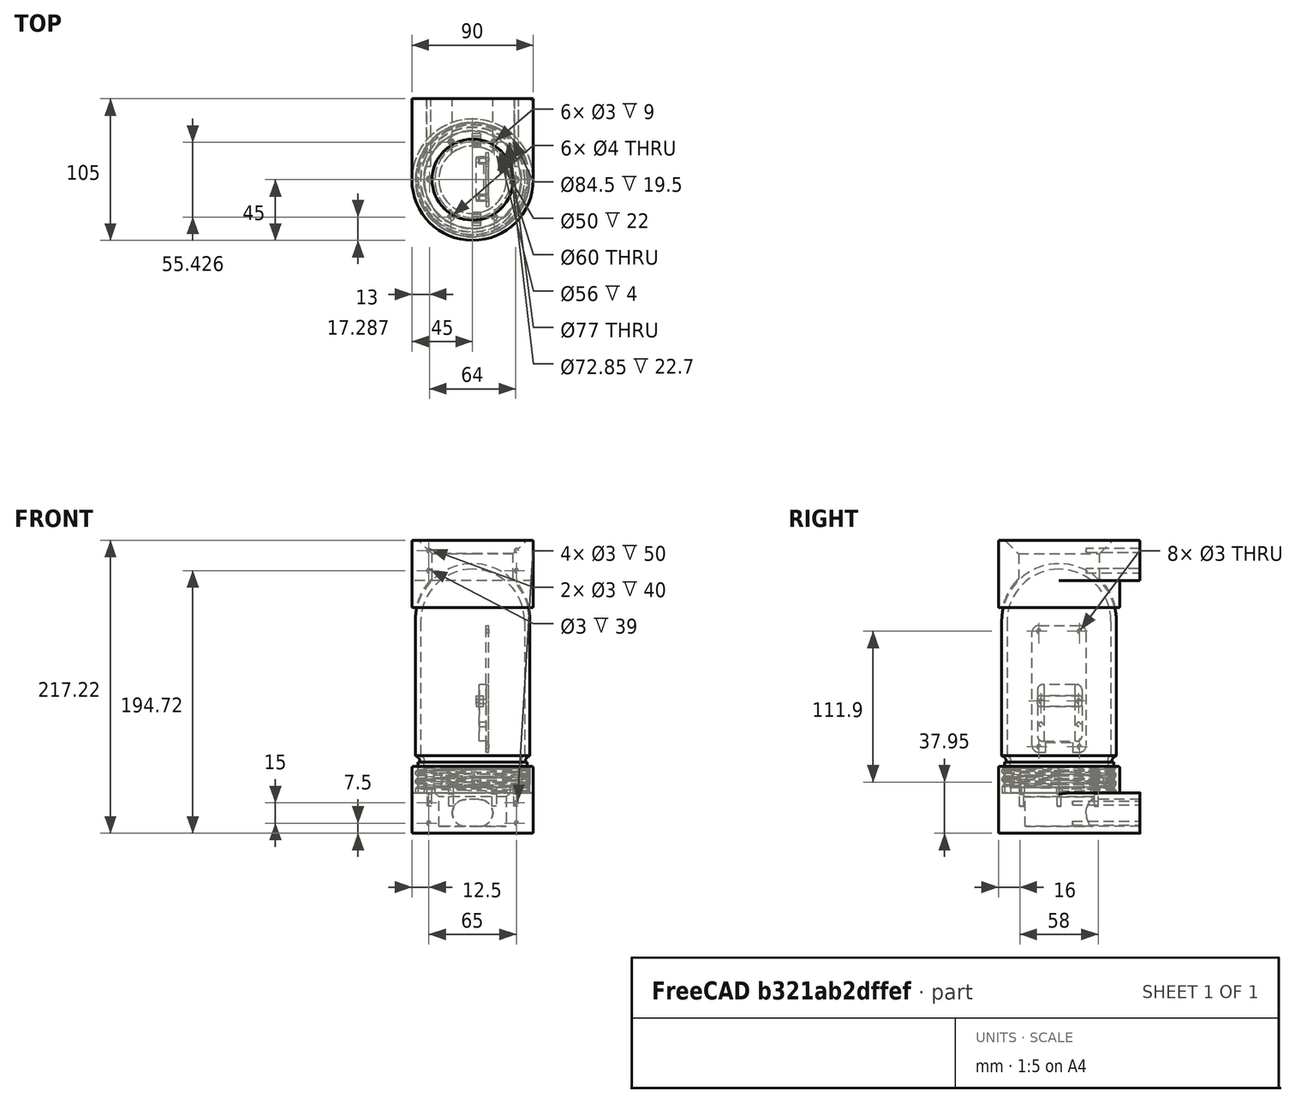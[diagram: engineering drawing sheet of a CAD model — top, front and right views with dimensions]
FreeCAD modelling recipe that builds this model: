
FCSTD DOCUMENT  (FreeCAD 0.20R)
Label: CrocSaintGerard_V6
License: All rights reserved
LicenseURL: http://en.wikipedia.org/wiki/All_rights_reserved
objects: Sketcher::SketchObject×46, PartDesign::Pocket×23, PartDesign::Fillet×21, PartDesign::Pad×19, PartDesign::Body×17, PartDesign::Chamfer×5, Mesh::Feature×4, TechDraw::DrawSVGTemplate×3, TechDraw::DrawViewPart×3, TechDraw::DrawPage×3, PartDesign::Revolution×2, Part::Helix×1, PartDesign::ShapeBinder×1, PartDesign::AdditivePipe×1, PartDesign::LinearPattern×1, PartDesign::Groove×1, App::VRMLObject×1, App::MeasureDistance×1
note: 210 computed .brp shape members not serialized (recipe doc carries the construction recipe); baked Part::Feature solids carry a one-line shape summary decoded from their .brp

FEATURE [Part::Helix] Helix
  Angle = 0
  AttacherType = Attacher::AttachEngine3D
  Height = 6.22
  LocalCoord = 0
  Pitch = 6.23
  Radius = 40.5
  SegmentLength = 1
  Style = 1
FEATURE [Sketcher::SketchObject] Sketch001  label="sketch_cylindre_base"
  FullyConstrained = true
  MapMode = 5
  Support = -> [XY_Plane]
  sketch-geometry (2):
    g0: Circle CenterX=0 CenterY=0 CenterZ=0 NormalX=0 NormalY=0 NormalZ=1 AngleXU=0 Radius=42.25
    g1: Circle CenterX=0 CenterY=0 CenterZ=0 NormalX=0 NormalY=0 NormalZ=1 AngleXU=0 Radius=45
  constraints (4):
    c: Coincident(g0,g-1)
    c: Coincident(g1,g0)
    c: Radius(g0) = 42.25
    c: Radius(g1) = 45
FEATURE [PartDesign::Pad] Pad  label="cylindre_base"
  Direction = (1,1,1)
  Length = 20
  Length2 = 100
  Profile = -> Sketch001
  Type = 0
FEATURE [Sketcher::SketchObject] Sketch002  label="sketch_profil_dent"
  FullyConstrained = true
  MapMode = 5
  Placement = pos=(0,0,0) rot=(1,0,0;1.5708rad)
  Support = -> [XZ_Plane]
  sketch-geometry (7):
    g0: LineSegment StartX=42.25 StartY=4.40427 StartZ=0 EndX=40.9557 EndY=3.11 EndZ=0
    g1: LineSegment StartX=40.9557 StartY=3.11 StartZ=0 EndX=40.9557 EndY=1.29427 EndZ=0
    g2: LineSegment StartX=40.9557 StartY=1.29427 StartZ=0 EndX=42.25 EndY=0 EndZ=0
    g3: LineSegment StartX=42.25 StartY=4.40427 StartZ=0 EndX=42.25 EndY=6.22 EndZ=0
    g4: LineSegment StartX=42.25 StartY=6.22 StartZ=0 EndX=43.25 EndY=6.22 EndZ=0
    g5: LineSegment StartX=43.25 StartY=6.22 StartZ=0 EndX=43.25 EndY=0 EndZ=0
    g6: LineSegment StartX=43.25 StartY=0 StartZ=0 EndX=42.25 EndY=0 EndZ=0
  constraints (21):
    c: Coincident(g0,g1)
    c: Vertical(g1)
    c: Coincident(g1,g2)
    c: DistanceX(g-2,g2) = 42.25
    c: PointOnObject(g2,g-1)
    c: Coincident(g0,g3)
    c: Vertical(g3)
    c: Coincident(g3,g4)
    c: Horizontal(g4)
    c: Coincident(g4,g5)
    c: PointOnObject(g5,g-1)
    c: Vertical(g5)
    c: Coincident(g5,g6)
    c: Coincident(g6,g2)
    c: DistanceX(g4,g4) = 1
    c: Equal(g3,g1)
    c: Equal(g2,g0)
    c: Angle(g2,g-1) = 0.785398
    c: Equal(g1,g3)
    c: DistanceY(g5,g5) = 6.22
    c: DistanceX(g-2,g0) = 42.25
FEATURE [PartDesign::ShapeBinder] ShapeBinder  label="ShapeBinder-helix"
  Support = -> [Helix]
  TraceSupport = false
FEATURE [PartDesign::AdditivePipe] AdditivePipe  label="filet"
  AuxilleryCurvelinear = true
  AuxillerySpineTangent = false
  BaseFeature = -> Pad
  Binormal = (0,0,0)
  Mode = 2
  Profile = -> Sketch002
  Spine = -> ShapeBinder
  SpineTangent = false
  Transformation = 0
  Transition = 0
FEATURE [PartDesign::LinearPattern] LinearPattern  label="ajout_filets"
  BaseFeature = -> AdditivePipe
  Direction = -> Z_Axis
  Length = 12.46
  Occurrences = 3
  Originals = -> [AdditivePipe]
  Overlap = 0
FEATURE [Sketcher::SketchObject] Sketch003  label="sketch_decoupe_filetage"
  FullyConstrained = true
  MapMode = 5
  Placement = pos=(0,0,0) rot=(1,0,0;1.5708rad)
  Support = -> [XZ_Plane]
  sketch-geometry (4):
    g0: LineSegment StartX=-90 StartY=29.5 StartZ=0 EndX=90 EndY=29.5 EndZ=0
    g1: LineSegment StartX=90 StartY=29.5 StartZ=0 EndX=90 EndY=19.5 EndZ=0
    g2: LineSegment StartX=90 StartY=19.5 StartZ=0 EndX=-90 EndY=19.5 EndZ=0
    g3: LineSegment StartX=-90 StartY=19.5 StartZ=0 EndX=-90 EndY=29.5 EndZ=0
  constraints (11):
    c: Coincident(g0,g1)
    c: Coincident(g1,g2)
    c: Coincident(g2,g3)
    c: Coincident(g3,g0)
    c: Horizontal(g2)
    c: Vertical(g1)
    c: Vertical(g3)
    c: DistanceY(g-1,g1) = 19.5
    c: Symmetric(g0,g0,g-2)
    c: DistanceY(g1,g1) = 10
    c: DistanceX(g0,g0) = 180
FEATURE [PartDesign::Pocket] Pocket  label="decoupe_filetage"
  BaseFeature = -> LinearPattern
  Length = 200
  Length2 = 100
  Midplane = true
  Profile = -> Sketch003
  Type = 0
FEATURE [Sketcher::SketchObject] Sketch008  label="sketch_enceinte_verre"
  FullyConstrained = true
  MapMode = 5
  Support = -> [XY_Plane003]
  sketch-geometry (11):
    g0: ArcOfCircle CenterX=-127.4 CenterY=0 CenterZ=0 NormalX=0 NormalY=0 NormalZ=1 AngleXU=0 Radius=42.5 StartAngle=1.5708 EndAngle=3.14159
    g1: ArcOfCircle CenterX=-127.4 CenterY=0 CenterZ=0 NormalX=0 NormalY=0 NormalZ=1 AngleXU=0 Radius=38.5 StartAngle=1.5708 EndAngle=3.14159
    g2: LineSegment StartX=-127.4 StartY=38.5 StartZ=0 EndX=-27.4 EndY=38.5 EndZ=0
    g3: ArcOfCircle CenterX=-24.2871 CenterY=39.1905 CenterZ=0 NormalX=0 NormalY=0 NormalZ=1 AngleXU=0 Radius=3.18854 StartAngle=3.35987 EndAngle=5.2334
    g4: LineSegment StartX=-22.7 StartY=36.425 StartZ=0 EndX=0 EndY=36.425 EndZ=0
    g5: LineSegment StartX=-127.4 StartY=42.5 StartZ=0 EndX=-27.4 EndY=42.5 EndZ=0
    g6: ArcOfCircle CenterX=-22.7 CenterY=43.802 CenterZ=0 NormalX=0 NormalY=0 NormalZ=1 AngleXU=0 Radius=4.87701 StartAngle=3.41184 EndAngle=4.71239
    g7: LineSegment StartX=-22.7 StartY=38.925 StartZ=0 EndX=-22.7 EndY=40.425 EndZ=0
    g8: LineSegment StartX=-22.7 StartY=40.425 StartZ=0 EndX=0 EndY=40.425 EndZ=0
    g9: LineSegment StartX=0 StartY=40.425 StartZ=0 EndX=0 EndY=36.425 EndZ=0
    g10: LineSegment StartX=-165.9 StartY=4.7e-15 StartZ=0 EndX=-169.9 EndY=5.2e-15 EndZ=0
  constraints (35):
    c: PointOnObject(g0,g-1)
    c: PointOnObject(g0,g-1)
    c: Coincident(g1,g0)
    c: PointOnObject(g1,g-1)
    c: Angle(g1) = 1.5708
    c: Angle(g0) = 1.5708
    c: Tangent(g1,g2) = 1.5708
    c: Coincident(g3,g2)
    c: Coincident(g4,g3)
    c: PointOnObject(g4,g-2)
    c: Horizontal(g4)
    c: Coincident(g5,g0)
    c: Horizontal(g5)
    c: Coincident(g6,g5)
    c: Coincident(g6,g7)
    c: Coincident(g7,g8)
    c: PointOnObject(g8,g-2)
    c: Horizontal(g8)
    c: Coincident(g8,g9)
    c: Coincident(g9,g4)
    c: Coincident(g10,g0)
    c: DistanceX(g10,g10) = 4
    c: Radius(g0) = 42.5
    c: Coincident(g1,g10)
    c: DistanceY(g9,g9) = 4
    c: Perpendicular(g6,g7)
    c: Vertical(g7)
    c: DistanceY(g-1,g4) = 36.425
    c: Equal(g4,g8)
    c: DistanceX(g8,g8) = 22.7
    c: DistanceX(g-2,g5) = -27.4
    c: Equal(g2,g5)
    c: PointOnObject(g3,g6)
    c: DistanceY(g7,g7) = 1.5
    c: DistanceX(g5,g5) = 100
FEATURE [PartDesign::Revolution] Revolution  label="revolution_enceinte_verre"
  AllowMultiFace = false
  Angle = 360
  Axis = (1,0,0)
  Base = (0,0,0)
  Profile = -> Sketch008
  ReferenceAxis = -> Sketch008 [H_Axis]
FEATURE [PartDesign::Body] Body003  label="enceinte_verre"
  Group = -> [Sketch008,Revolution]
  Origin = -> Origin003
  Placement = pos=(-3.8e-15,0,-1.78e-14) rot=(0,1,0;1.5708rad)
  Tip = -> Revolution
FEATURE [Sketcher::SketchObject] Sketch  label="sketch_base"
  ExternalGeometry = -> [Pocket]
  FullyConstrained = true
  MapMode = 5
  Placement = pos=(0,0,0) rot=(1,0,0;3.14159rad)
  Support = -> [Pocket]
  sketch-geometry (4):
    g0: ArcOfCircle CenterX=0 CenterY=0 CenterZ=0 NormalX=0 NormalY=0 NormalZ=1 AngleXU=0 Radius=45 StartAngle=0 EndAngle=3.14159
    g1: LineSegment StartX=-45 StartY=5.5e-15 StartZ=0 EndX=-45 EndY=-60 EndZ=0
    g2: LineSegment StartX=-45 StartY=-60 StartZ=0 EndX=45 EndY=-60 EndZ=0
    g3: LineSegment StartX=45 StartY=-60 StartZ=0 EndX=45 EndY=0 EndZ=0
  constraints (11):
    c: Coincident(g0,g-1)
    c: PointOnObject(g0,g-1)
    c: PointOnObject(g0,g-1)
    c: Tangent(g0,g1) = -1.5708
    c: Coincident(g1,g2)
    c: Horizontal(g2)
    c: Coincident(g2,g3)
    c: Coincident(g3,g0)
    c: Vertical(g3)
    c: Radius(g0) = 45
    c: DistanceY(g1,g1) = 60
FEATURE [PartDesign::Pad] Pad001  label="base"
  BaseFeature = -> Pocket
  Direction = (1,1,1)
  Length = 30
  Length2 = 100
  Profile = -> Sketch
  Type = 0
FEATURE [Sketcher::SketchObject] Sketch009  label="sketch_passage_fils"
  FullyConstrained = true
  MapMode = 5
  Support = -> [Pad001]
  sketch-geometry (1):
    g0: Circle CenterX=0 CenterY=0 CenterZ=0 NormalX=0 NormalY=0 NormalZ=1 AngleXU=0 Radius=25
  constraints (2):
    c: Coincident(g0,g-1)
    c: Radius(g0) = 25
FEATURE [PartDesign::Pocket] Pocket001  label="passage_fils"
  BaseFeature = -> Pad001
  Length = 25
  Length2 = 100
  Profile = -> Sketch009
  Type = 0
FEATURE [Sketcher::SketchObject] Sketch010  label="sketch_passage_fils_vertical"
  ExternalGeometry = -> [Pocket001]
  FullyConstrained = true
  MapMode = 5
  Placement = pos=(0,60,0) rot=(0,0.707107,0.707107;3.14159rad)
  Support = -> [Pocket001]
  sketch-geometry (4):
    g0: ArcOfCircle CenterX=-5 CenterY=-15 CenterZ=0 NormalX=0 NormalY=0 NormalZ=1 AngleXU=0 Radius=10 StartAngle=1.5708 EndAngle=4.71239
    g1: ArcOfCircle CenterX=5 CenterY=-15 CenterZ=0 NormalX=0 NormalY=0 NormalZ=1 AngleXU=0 Radius=10 StartAngle=4.71239 EndAngle=7.85398
    g2: LineSegment StartX=-5 StartY=-25 StartZ=0 EndX=5 EndY=-25 EndZ=0
    g3: LineSegment StartX=-5 StartY=-5 StartZ=0 EndX=5 EndY=-5 EndZ=0
  constraints (9):
    c: Tangent(g0,g3) = 1.5708
    c: Tangent(g0,g2) = -1.5708
    c: Tangent(g2,g1) = -1.5708
    c: Tangent(g3,g1) = 1.5708
    c: Equal(g0,g1)
    c: Symmetric(g0,g1,g-2)
    c: Distance(g1,g-3) = 5
    c: DistanceY(g-1,g1) = -5
    c: DistanceX(g2,g2) = 10
FEATURE [PartDesign::Pocket] Pocket002  label="passage_fils_vertical"
  BaseFeature = -> Pocket001
  Length = 60
  Length2 = 100
  Profile = -> Sketch010
  Type = 0
FEATURE [Sketcher::SketchObject] Sketch011  label="sketch_vis_fixation"
  ExternalGeometry = -> [Pocket002]
  FullyConstrained = true
  MapMode = 5
  Placement = pos=(0,60,0) rot=(0,0.707107,0.707107;3.14159rad)
  Support = -> [Pocket002]
  sketch-geometry (4):
    g0: Circle CenterX=-32.5 CenterY=-7.5 CenterZ=0 NormalX=0 NormalY=0 NormalZ=1 AngleXU=0 Radius=1.5
    g1: Circle CenterX=32.5 CenterY=-7.5 CenterZ=0 NormalX=0 NormalY=0 NormalZ=1 AngleXU=0 Radius=1.5
    g2: Circle CenterX=-32.5 CenterY=-22.5 CenterZ=0 NormalX=0 NormalY=0 NormalZ=1 AngleXU=0 Radius=1.5
    g3: Circle CenterX=32.5 CenterY=-22.5 CenterZ=0 NormalX=0 NormalY=0 NormalZ=1 AngleXU=0 Radius=1.5
  constraints (10):
    c: Symmetric(g1,g0,g-2)
    c: DistanceY(g-1,g0) = -7.5
    c: Distance(g0,g1) = 65
    c: Radius(g0) = 1.5
    c: Equal(g0,g1)
    c: Symmetric(g3,g2,g-2)
    c: Radius(g2) = 1.5
    c: Equal(g2,g3)
    c: Distance(g3,g2) = 65
    c: Distance(g3,g-3) = 7.5
FEATURE [PartDesign::Pocket] Pocket003  label="vis_fixation"
  BaseFeature = -> Pocket002
  Length = 50
  Length2 = 100
  Profile = -> Sketch011
  Type = 0
FEATURE [PartDesign::Chamfer] Chamfer
  Angle = 45
  Base = -> Pocket003 [Edge95]
  BaseFeature = -> Pocket003
  ChamferType = 0
  FlipDirection = false
  Size = 3
  Size2 = 1
  SupportTransform = false
FEATURE [Sketcher::SketchObject] Sketch012  label="sketch_vis_montage_interieur"
  FullyConstrained = true
  MapMode = 5
  Support = -> [Chamfer]
  sketch-geometry (13):
    g0: LineSegment StartX=-16 StartY=27.7128 StartZ=0 EndX=-32 EndY=-3.3857e-12 EndZ=0
    g1: LineSegment StartX=-32 StartY=-3.3857e-12 StartZ=0 EndX=-16 EndY=-27.7128 EndZ=0
    g2: LineSegment StartX=-16 StartY=-27.7128 StartZ=0 EndX=16 EndY=-27.7128 EndZ=0
    g3: LineSegment StartX=16 StartY=-27.7128 StartZ=0 EndX=32 EndY=9.738e-12 EndZ=0
    g4: LineSegment StartX=32 StartY=9.738e-12 StartZ=0 EndX=16 EndY=27.7128 EndZ=0
    g5: LineSegment StartX=16 StartY=27.7128 StartZ=0 EndX=-16 EndY=27.7128 EndZ=0
    g6: Circle CenterX=0 CenterY=0 CenterZ=0 NormalX=0 NormalY=0 NormalZ=1 AngleXU=0 Radius=32
    g7: Circle CenterX=-16 CenterY=27.7128 CenterZ=0 NormalX=0 NormalY=0 NormalZ=1 AngleXU=0 Radius=1.5
    g8: Circle CenterX=16 CenterY=27.7128 CenterZ=0 NormalX=0 NormalY=0 NormalZ=1 AngleXU=0 Radius=1.5
    g9: Circle CenterX=-32 CenterY=-3.3857e-12 CenterZ=0 NormalX=0 NormalY=0 NormalZ=1 AngleXU=0 Radius=1.5
    g10: Circle CenterX=32 CenterY=9.738e-12 CenterZ=0 NormalX=0 NormalY=0 NormalZ=1 AngleXU=0 Radius=1.5
    g11: Circle CenterX=16 CenterY=-27.7128 CenterZ=0 NormalX=0 NormalY=0 NormalZ=1 AngleXU=0 Radius=1.5
    g12: Circle CenterX=-16 CenterY=-27.7128 CenterZ=0 NormalX=0 NormalY=0 NormalZ=1 AngleXU=0 Radius=1.5
  constraints (28):
    c: Coincident(g0,g1)
    c: Coincident(g1,g2)
    c: Coincident(g2,g3)
    c: Coincident(g3,g4)
    c: Coincident(g4,g5)
    c: Coincident(g5,g0)
    c: Equal(g0, g1-g5) x5
    c: PointOnObject(g0,g6)
    c: PointOnObject(g1,g6)
    c: PointOnObject(g2,g6)
    c: PointOnObject(g3,g6)
    c: PointOnObject(g4,g6)
    c: PointOnObject(g5,g6)
    c: Coincident(g6,g-1)
    c: Horizontal(g5)
    c: Radius(g6) = 32
    c: Coincident(g7,g0)
    c: Coincident(g8,g4)
    c: Coincident(g9,g0)
    c: Coincident(g10,g3)
    c: Coincident(g11,g2)
    c: Coincident(g12,g1)
    c: Radius(g11) = 1.5
    c: Equal(g11,g12)
    c: Equal(g11,g9)
    c: Equal(g11,g7)
    c: Equal(g11,g8)
    c: Equal(g11,g10)
FEATURE [PartDesign::Pocket] Pocket004  label="vis_montage_interieur"
  BaseFeature = -> Chamfer
  Length = 10
  Length2 = 100
  Profile = -> Sketch012
  Type = 0
FEATURE [PartDesign::Chamfer] Chamfer001
  Angle = 45
  Base = -> Pocket004 [Edge3,Edge2,Edge4,Edge6,Edge8,Edge7]
  BaseFeature = -> Pocket004
  ChamferType = 0
  FlipDirection = false
  Size = 1
  Size2 = 1
  SupportTransform = false
FEATURE [Mesh::Feature] Mesh  label="fixation_enceinte_verre (Meshed)"
FEATURE [Sketcher::SketchObject] Sketch013
  FullyConstrained = true
  MapMode = 5
  Placement = pos=(0,0,0) rot=(0.57735,0.57735,0.57735;2.0944rad)
  Support = -> [YZ_Plane004]
  sketch-geometry (4):
    g0: ArcOfCircle CenterX=0 CenterY=128 CenterZ=0 NormalX=0 NormalY=0 NormalZ=1 AngleXU=0 Radius=43 StartAngle=2.39448 EndAngle=2.92551
    g1: LineSegment StartX=-42 StartY=137.22 StartZ=0 EndX=-45 EndY=137.22 EndZ=0
    g2: LineSegment StartX=-45 StartY=137.22 StartZ=0 EndX=-45 EndY=157.22 EndZ=0
    g3: LineSegment StartX=-45 StartY=157.22 StartZ=0 EndX=-31.5471 EndY=157.22 EndZ=0
  constraints (13):
    c: PointOnObject(g0,g-2)
    c: Coincident(g0,g1)
    c: Coincident(g1,g2)
    c: Vertical(g2)
    c: Coincident(g2,g3)
    c: Coincident(g3,g0)
    c: Horizontal(g3)
    c: Horizontal(g1)
    c: Radius(g0) = 43
    c: DistanceY(g2,g2) = 20
    c: DistanceX(g-2,g1) = -45
    c: DistanceY(g-1,g0) = 128
    c: DistanceX(g1,g1) = 3
FEATURE [PartDesign::Revolution] Revolution001
  Angle = 360
  Axis = (-2e-16,3e-16,1)
  Base = (0,0,0)
  Placement = pos=(0,0,0) rot=(0.57735,0.57735,0.57735;2.0944rad)
  Profile = -> Sketch013
  ReferenceAxis = -> Sketch013 [V_Axis]
FEATURE [Sketcher::SketchObject] Sketch014
  ExternalGeometry = -> [Revolution001]
  FullyConstrained = true
  MapMode = 5
  Placement = pos=(-6.92e-14,4.4e-14,157.22) rot=(0,0,-1;1.5708rad)
  Support = -> [Revolution001]
  sketch-geometry (4):
    g0: ArcOfCircle CenterX=0 CenterY=0 CenterZ=0 NormalX=0 NormalY=0 NormalZ=1 AngleXU=0 Radius=45 StartAngle=4.71239 EndAngle=7.85398
    g1: LineSegment StartX=1.38e-14 StartY=45 StartZ=0 EndX=-60 EndY=45 EndZ=0
    g2: LineSegment StartX=-60 StartY=45 StartZ=0 EndX=-60 EndY=-45 EndZ=0
    g3: LineSegment StartX=-60 StartY=-45 StartZ=0 EndX=-7.1e-15 EndY=-45 EndZ=0
  constraints (10):
    c: Coincident(g0,g-1)
    c: PointOnObject(g0,g-3)
    c: PointOnObject(g0,g-2)
    c: PointOnObject(g0,g-2)
    c: Tangent(g0,g1) = -1.5708
    c: Coincident(g1,g2)
    c: Coincident(g2,g3)
    c: Coincident(g3,g0)
    c: Symmetric(g2,g1,g-1)
    c: DistanceX(g-2,g1) = -60
FEATURE [PartDesign::Pad] Pad002
  BaseFeature = -> Revolution001
  Direction = (1,1,1)
  Length = 30
  Length2 = 100
  Placement = pos=(0,0,0) rot=(0.57735,0.57735,0.57735;2.0944rad)
  Profile = -> Sketch014
  Type = 0
FEATURE [Sketcher::SketchObject] Sketch015
  ExternalGeometry = -> [Pad002]
  FullyConstrained = true
  MapMode = 5
  Placement = pos=(0,0,0) rot=(0.57735,0.57735,0.57735;2.0944rad)
  Support = -> [YZ_Plane004]
  sketch-geometry (3):
    g0: ArcOfCircle CenterX=2.84e-14 CenterY=128 CenterZ=0 NormalX=0 NormalY=0 NormalZ=1 AngleXU=0 Radius=43 StartAngle=1.5708 EndAngle=2.39448
    g1: LineSegment StartX=-31.5471 StartY=157.22 StartZ=0 EndX=3.6e-15 EndY=157.22 EndZ=0
    g2: LineSegment StartX=3.6e-15 StartY=157.22 StartZ=0 EndX=3.6e-15 EndY=171 EndZ=0
  constraints (8):
    c: Coincident(g0,g-3)
    c: Coincident(g0,g-3)
    c: PointOnObject(g0,g-2)
    c: Coincident(g0,g1)
    c: Coincident(g1,g2)
    c: Coincident(g2,g0)
    c: Vertical(g2)
    c: Horizontal(g1)
FEATURE [PartDesign::Groove] Groove
  Angle = 360
  Axis = (-2e-16,3e-16,1)
  Base = (0,0,0)
  BaseFeature = -> Pad002
  Placement = pos=(0,0,0) rot=(0.57735,0.57735,0.57735;2.0944rad)
  Profile = -> Sketch015
  ReferenceAxis = -> Sketch015 [V_Axis]
  Reversed = true
FEATURE [PartDesign::Fillet] Fillet
  Base = -> Chamfer001 [Edge116,Edge168,Edge182,Edge171,Edge181,Edge166]
  BaseFeature = -> Chamfer001
  Radius = 1
  SupportTransform = false
FEATURE [PartDesign::Body] Body  label="fixation_enceinte_verre"
  Group = -> [Sketch001,Pad,Sketch002,ShapeBinder,AdditivePipe,LinearPattern,Sketch003,Pocket,Sketch,Pad001,Sketch009,Pocket001,Sketch010,Pocket002,Sketch011,Pocket003,Chamfer,Sketch012,Pocket004,Chamfer001,Fillet]
  Origin = -> Origin
  Tip = -> Fillet
FEATURE [Sketcher::SketchObject] Sketch019
  FullyConstrained = true
  MapMode = 5
  Support = -> [XY_Plane005]
  sketch-geometry (15):
    g0: Circle CenterX=0 CenterY=0 CenterZ=0 NormalX=0 NormalY=0 NormalZ=1 AngleXU=0 Radius=28
    g1: Circle CenterX=0 CenterY=0 CenterZ=0 NormalX=0 NormalY=0 NormalZ=1 AngleXU=0 Radius=36
    g2: LineSegment StartX=-32 StartY=0 StartZ=0 EndX=-16 EndY=-27.7128 EndZ=0
    g3: LineSegment StartX=-16 StartY=-27.7128 StartZ=0 EndX=16 EndY=-27.7128 EndZ=0
    g4: LineSegment StartX=16 StartY=-27.7128 StartZ=0 EndX=32 EndY=-3.2792e-12 EndZ=0
    g5: LineSegment StartX=32 StartY=-3.2792e-12 StartZ=0 EndX=16 EndY=27.7128 EndZ=0
    g6: LineSegment StartX=16 StartY=27.7128 StartZ=0 EndX=-16 EndY=27.7128 EndZ=0
    g7: LineSegment StartX=-16 StartY=27.7128 StartZ=0 EndX=-32 EndY=0 EndZ=0
    g8: Circle CenterX=0 CenterY=0 CenterZ=0 NormalX=0 NormalY=0 NormalZ=1 AngleXU=0 Radius=32
    g9: Circle CenterX=-16 CenterY=27.7128 CenterZ=0 NormalX=0 NormalY=0 NormalZ=1 AngleXU=0 Radius=2
    g10: Circle CenterX=16 CenterY=27.7128 CenterZ=0 NormalX=0 NormalY=0 NormalZ=1 AngleXU=0 Radius=2
    g11: Circle CenterX=32 CenterY=-3.2792e-12 CenterZ=0 NormalX=0 NormalY=0 NormalZ=1 AngleXU=0 Radius=2
    g12: Circle CenterX=16 CenterY=-27.7128 CenterZ=0 NormalX=0 NormalY=0 NormalZ=1 AngleXU=0 Radius=2
    g13: Circle CenterX=-16 CenterY=-27.7128 CenterZ=0 NormalX=0 NormalY=0 NormalZ=1 AngleXU=0 Radius=2
    g14: Circle CenterX=-32 CenterY=0 CenterZ=0 NormalX=0 NormalY=0 NormalZ=1 AngleXU=0 Radius=2
  constraints (28):
    c: Radius(g0) = 28
    c: Radius(g1) = 36
    c: Coincident(g0,g1)
    c: Coincident(g0,g-1)
    c: Coincident(g2,g3)
    c: Coincident(g3,g4)
    c: Coincident(g4,g5)
    c: Coincident(g5,g6)
    c: Coincident(g6,g7)
    c: Coincident(g7,g2)
    c: Equal(g2, g3-g7) x5
    c: PointOnObject(g2,g8)
    c: PointOnObject(g3,g8)
    c: PointOnObject(g4,g8)
    c: PointOnObject(g5,g8)
    c: PointOnObject(g6,g8)
    c: PointOnObject(g7,g8)
    c: Coincident(g8,g0)
    c: PointOnObject(g7,g-1)
    c: Radius(g8) = 32
    c: Coincident(g9,g6)
    c: Coincident(g10,g5)
    c: Coincident(g11,g4)
    c: Coincident(g12,g3)
    c: Coincident(g13,g2)
    c: Coincident(g14,g2)
    c: Radius(g9) = 2
    c: Equal(g9, g10-g14) x5
FEATURE [PartDesign::Pad] Pad003
  Direction = (1,1,1)
  Length = 4
  Length2 = 100
  Profile = -> Sketch019
  Type = 0
FEATURE [Sketcher::SketchObject] Sketch021
  FullyConstrained = true
  MapMode = 5
  Placement = pos=(-1.179e-13,8.24e-14,187.22) rot=(0,0,-1;1.5708rad)
  Support = -> [Pad002]
  sketch-geometry (1):
    g0: Circle CenterX=0 CenterY=0 CenterZ=0 NormalX=0 NormalY=0 NormalZ=1 AngleXU=0 Radius=30
  constraints (2):
    c: Coincident(g0,g-1)
    c: Radius(g0) = 30
FEATURE [PartDesign::Pocket] Pocket009
  BaseFeature = -> Groove
  Length = 46
  Length2 = 100
  Placement = pos=(0,0,0) rot=(0.57735,0.57735,0.57735;2.0944rad)
  Profile = -> Sketch021
  Type = 0
FEATURE [Sketcher::SketchObject] Sketch022
  FullyConstrained = false
  MapMode = 5
  Placement = pos=(2.7e-14,60,-7e-14) rot=(0.57735,0.57735,0.57735;4.18879rad)
  sketch-geometry (4):
    g0: Circle CenterX=164.72 CenterY=32.5 CenterZ=0 NormalX=0 NormalY=0 NormalZ=1 AngleXU=0 Radius=1.5
    g1: Circle CenterX=179.72 CenterY=32.5 CenterZ=0 NormalX=0 NormalY=0 NormalZ=1 AngleXU=0 Radius=1.5
    g2: Circle CenterX=164.72 CenterY=-32.5 CenterZ=0 NormalX=0 NormalY=0 NormalZ=1 AngleXU=0 Radius=1.5
    g3: Circle CenterX=179.72 CenterY=-32.5 CenterZ=0 NormalX=0 NormalY=0 NormalZ=1 AngleXU=0 Radius=1.5
  constraints (8):
    c: Symmetric(g3,g1,g-1)
    c: Symmetric(g0,g2,g-1)
    c: Distance(g0,g2) = 65
    c: Distance(g3,g1) = 65
    c: Radius(g0) = 1.5
    c: Equal(g0,g1)
    c: Equal(g0,g2)
    c: Equal(g0,g3)
FEATURE [PartDesign::Pocket] Pocket010
  BaseFeature = -> Pocket009
  Length = 40
  Length2 = 100
  Placement = pos=(0,0,0) rot=(0.57735,0.57735,0.57735;2.0944rad)
  Profile = -> Sketch022
  Type = 0
FEATURE [PartDesign::Fillet] Fillet001
  Base = -> Pocket010 [Edge10,Edge27]
  BaseFeature = -> Pocket010
  Placement = pos=(0,0,0) rot=(0.57735,0.57735,0.57735;2.0944rad)
  Radius = 1
  SupportTransform = false
FEATURE [PartDesign::Fillet] Fillet002
  Base = -> Fillet001 [Edge5,Edge21]
  BaseFeature = -> Fillet001
  Placement = pos=(0,0,0) rot=(0.57735,0.57735,0.57735;2.0944rad)
  Radius = 1
  SupportTransform = false
FEATURE [PartDesign::Chamfer] Chamfer002
  Angle = 45
  Base = -> Fillet002 [Edge19]
  BaseFeature = -> Fillet002
  ChamferType = 0
  FlipDirection = false
  Placement = pos=(0,0,0) rot=(0.57735,0.57735,0.57735;2.0944rad)
  Size = 10
  Size2 = 1
  SupportTransform = false
FEATURE [PartDesign::Fillet] Fillet003
  Base = -> Chamfer002 [Edge2]
  BaseFeature = -> Chamfer002
  Placement = pos=(0,0,0) rot=(0.57735,0.57735,0.57735;2.0944rad)
  Radius = 1
  SupportTransform = false
FEATURE [PartDesign::Fillet] Fillet004
  Base = -> Fillet003 [Edge46,Edge5,Edge34]
  BaseFeature = -> Fillet003
  Placement = pos=(0,0,0) rot=(0.57735,0.57735,0.57735;2.0944rad)
  Radius = 1
  SupportTransform = false
FEATURE [PartDesign::Body] Body004  label="tete"
  Group = -> [Sketch013,Revolution001,Sketch014,Pad002,Sketch015,Groove,Sketch021,Pocket009,Sketch022,Pocket010,Fillet001,Fillet002,Chamfer002,Fillet003,Fillet004]
  Origin = -> Origin004
  Tip = -> Fillet004
FEATURE [Mesh::Feature] Mesh001  label="tete (Meshed)"
FEATURE [Sketcher::SketchObject] Sketch005
  FullyConstrained = false
  MapMode = 5
  Placement = pos=(0,0,0) rot=(0.57735,0.57735,0.57735;2.0944rad)
  Support = -> [YZ_Plane002]
  sketch-geometry (8):
    g0: LineSegment StartX=-17 StartY=-5 StartZ=0 EndX=-11.875 EndY=-5 EndZ=0
    g1: LineSegment StartX=-11.875 StartY=-5 StartZ=0 EndX=-11.875 EndY=-1.6 EndZ=0
    g2: LineSegment StartX=-11.875 StartY=-1.6 StartZ=0 EndX=10.875 EndY=-1.6 EndZ=0
    g3: LineSegment StartX=10.875 StartY=-1.6 StartZ=0 EndX=10.875 EndY=-5 EndZ=0
    g4: LineSegment StartX=10.875 StartY=-5 StartZ=0 EndX=16 EndY=-5 EndZ=0
    g5: LineSegment StartX=16 StartY=-5 StartZ=0 EndX=16 EndY=-7 EndZ=0
    g6: LineSegment StartX=16 StartY=-7 StartZ=0 EndX=-17 EndY=-7 EndZ=0
    g7: LineSegment StartX=-17 StartY=-7 StartZ=0 EndX=-17 EndY=-5 EndZ=0
  constraints (24):
    c: Horizontal(g0)
    c: Coincident(g0,g1)
    c: Vertical(g1)
    c: Coincident(g1,g2)
    c: Horizontal(g2)
    c: Coincident(g2,g3)
    c: Vertical(g3)
    c: Coincident(g3,g4)
    c: Horizontal(g4)
    c: Coincident(g4,g5)
    c: Vertical(g5)
    c: Coincident(g5,g6)
    c: Horizontal(g6)
    c: Coincident(g6,g7)
    c: Coincident(g7,g0)
    c: Vertical(g7)
    c: DistanceY(g7,g7) = 2
    c: DistanceY(g1,g1) = 3.4
    c: DistanceX(g2,g2) = 22.75
    c: DistanceX(g0,g0) = 5.125
    c: Equal(g0,g4)
    c: Equal(g5,g7)
    c: DistanceY(g-1,g0) = -5
    c: DistanceX(g-2,g6) = -17
FEATURE [PartDesign::Pad] Pad010
  AllowMultiFace = false
  Direction = (1,1,1)
  Length = 8
  Length2 = 100
  Placement = pos=(0,0,0) rot=(0.57735,0.57735,0.57735;2.0944rad)
  Profile = -> Sketch005
  Type = 0
FEATURE [Sketcher::SketchObject] Sketch006
  ExternalGeometry = -> [Pad010]
  FullyConstrained = true
  MapMode = 5
  Placement = pos=(2e-15,-3.1e-15,-7) rot=(0.707107,0.707107,0;3.14159rad)
  Support = -> [Pad010]
  sketch-geometry (2):
    g0: Circle CenterX=-14.5 CenterY=4 CenterZ=0 NormalX=0 NormalY=0 NormalZ=1 AngleXU=0 Radius=1.5
    g1: Circle CenterX=13.5 CenterY=4 CenterZ=0 NormalX=0 NormalY=0 NormalZ=1 AngleXU=0 Radius=1.5
  constraints (6):
    c: Radius(g1) = 1.5
    c: Equal(g1,g0)
    c: DistanceY(g-1,g1) = 4
    c: DistanceY(g-1,g0) = 4
    c: Distance(g0,g-3) = 2.5
    c: Distance(g1,g-4) = 2.5
FEATURE [PartDesign::Pocket] Pocket013
  AllowMultiFace = false
  BaseFeature = -> Pad010
  Length = 5
  Length2 = 100
  Placement = pos=(0,0,0) rot=(0.57735,0.57735,0.57735;2.0944rad)
  Profile = -> Sketch006
  Type = 0
FEATURE [PartDesign::Fillet] Fillet007
  Base = -> Pocket013 [Edge8,Edge7,Edge19,Edge13]
  BaseFeature = -> Pocket013
  Placement = pos=(0,0,0) rot=(0.57735,0.57735,0.57735;2.0944rad)
  Radius = 2
  SupportTransform = false
FEATURE [PartDesign::Body] Body002  label="Attache"
  Group = -> [Sketch005,Pad010,Sketch006,Pocket013,Fillet007]
  Origin = -> Origin002
  Placement = pos=(9.75,-3e-15,64) rot=(0.707107,0,0.707107;3.14159rad)
  Tip = -> Fillet007
FEATURE [App::VRMLObject] CroqueLivreSaintGerard2021_V1
  Placement = pos=(-16,93.8,-73.5) rot=(0,1,0;-1.5708rad)
  Resources = CroqueLivreSaintGerard2021_V1/CP_Radial_D12.5mm_P5.00mm.wrl | CroqueLivreSaintGerard2021_V1/ | CroqueLivreSaintGerard2021_V1/ | CroqueLivreSaintGerard2021_V1/ | CroqueLivreSaintGerard2021_V1/ | CroqueLivreSaintGerard2021_V1/ | CroqueLivreSaintGerard2021_V1/ | CroqueLivreSaintGerard2021_V1/ | CroqueLivreSaintGerard2021_V1/ | CroqueLivreSaintGerard2021_V1/ | CroqueLivreSaintGerard2021_V1/ | CroqueLivreSaintGerard2021_V1/
FEATURE [Sketcher::SketchObject] Sketch025
  FullyConstrained = true
  MapMode = 5
  Support = -> [XY_Plane006]
  sketch-geometry (17):
    g0: LineSegment StartX=-47 StartY=20 StartZ=0 EndX=47 EndY=20 EndZ=0
    g1: LineSegment StartX=47 StartY=20 StartZ=0 EndX=47 EndY=-20 EndZ=0
    g2: LineSegment StartX=47 StartY=-20 StartZ=0 EndX=-47 EndY=-20 EndZ=0
    g3: LineSegment StartX=-39.75 StartY=18.75 StartZ=0 EndX=39.75 EndY=18.75 EndZ=0
    g4: LineSegment StartX=39.75 StartY=18.75 StartZ=0 EndX=39.75 EndY=-18.75 EndZ=0
    g5: LineSegment StartX=39.75 StartY=-18.75 StartZ=0 EndX=-39.75 EndY=-18.75 EndZ=0
    g6: LineSegment StartX=-39.75 StartY=-18.75 StartZ=0 EndX=-39.75 EndY=18.75 EndZ=0
    g7: Circle CenterX=-42.85 CenterY=15 CenterZ=0 NormalX=0 NormalY=0 NormalZ=1 AngleXU=0 Radius=1.5
    g8: Circle CenterX=-42.85 CenterY=-15 CenterZ=0 NormalX=0 NormalY=0 NormalZ=1 AngleXU=0 Radius=1.5
    g9: Circle CenterX=42.85 CenterY=-15 CenterZ=0 NormalX=0 NormalY=0 NormalZ=1 AngleXU=0 Radius=1.5
    g10: Circle CenterX=42.85 CenterY=15 CenterZ=0 NormalX=0 NormalY=0 NormalZ=1 AngleXU=0 Radius=1.5
    g11: Circle CenterX=-42.85 CenterY=15 CenterZ=0 NormalX=0 NormalY=0 NormalZ=1 AngleXU=0 Radius=3
    g12: LineSegment StartX=-47 StartY=20 StartZ=0 EndX=-47 EndY=10 EndZ=0
    g13: LineSegment StartX=-47 StartY=10 StartZ=0 EndX=-39.75 EndY=10 EndZ=0
    g14: LineSegment StartX=-39.75 StartY=10 StartZ=0 EndX=-39.75 EndY=-10 EndZ=0
    g15: LineSegment StartX=-39.75 StartY=-10 StartZ=0 EndX=-47 EndY=-10 EndZ=0
    g16: LineSegment StartX=-47 StartY=-10 StartZ=0 EndX=-47 EndY=-20 EndZ=0
  constraints (44):
    c: Coincident(g0,g1)
    c: Coincident(g1,g2)
    c: Horizontal(g0)
    c: Horizontal(g2)
    c: Vertical(g1)
    c: Symmetric(g0,g1,g-1)
    c: DistanceY(g1,g1) = 40
    c: DistanceX(g0,g0) = 94
    c: Coincident(g3,g4)
    c: Coincident(g4,g5)
    c: Coincident(g5,g6)
    c: Coincident(g6,g3)
    c: Horizontal(g3)
    c: Horizontal(g5)
    c: Vertical(g4)
    c: Vertical(g6)
    c: Symmetric(g3,g4,g-1)
    c: DistanceY(g6,g6) = 37.5
    c: DistanceX(g3,g3) = 79.5
    c: Radius(g10) = 1.5
    c: Equal(g10,g9)
    c: Equal(g10,g8)
    c: Equal(g10,g7)
    c: Symmetric(g7,g8,g-1)
    c: Symmetric(g10,g9,g-1)
    c: Symmetric(g10,g7,g-2)
    c: Coincident(g11,g7)
    c: Radius(g11) = 3
    c: Coincident(g0,g12)
    c: Vertical(g12)
    c: Coincident(g12,g13)
    c: Horizontal(g13)
    c: Coincident(g13,g14)
    c: Vertical(g14)
    c: Coincident(g14,g15)
    c: Horizontal(g15)
    c: Coincident(g15,g16)
    c: Coincident(g16,g2)
    c: Vertical(g16)
    c: Symmetric(g15,g12,g-1)
    c: PointOnObject(g13,g6)
    c: DistanceY(g14,g14) = 20
    c: DistanceY(g-1,g7) = 15
    c: DistanceX(g-2,g7) = -42.85
FEATURE [PartDesign::Pad] Pad011
  AllowMultiFace = false
  Direction = (1,1,1)
  Length = 2
  Length2 = 100
  Profile = -> Sketch025
  Type = 0
FEATURE [PartDesign::Fillet] Fillet006
  Base = -> Pad011 [Edge8,Edge5,Edge11,Edge1]
  BaseFeature = -> Pad011
  Radius = 5
  SupportTransform = false
FEATURE [Sketcher::SketchObject] Sketch024
  ExternalGeometry = -> [Fillet006]
  FullyConstrained = true
  MapMode = 5
  Placement = pos=(0,0,0) rot=(1,0,0;3.14159rad)
  Support = -> [Fillet006]
  sketch-geometry (4):
    g0: LineSegment StartX=-38.75 StartY=12 StartZ=0 EndX=3.25 EndY=12 EndZ=0
    g1: LineSegment StartX=3.25 StartY=12 StartZ=0 EndX=3.25 EndY=-11 EndZ=0
    g2: LineSegment StartX=3.25 StartY=-11 StartZ=0 EndX=-38.75 EndY=-11 EndZ=0
    g3: LineSegment StartX=-38.75 StartY=-11 StartZ=0 EndX=-38.75 EndY=12 EndZ=0
  constraints (12):
    c: Coincident(g0,g1)
    c: Coincident(g1,g2)
    c: Coincident(g2,g3)
    c: Coincident(g3,g0)
    c: Horizontal(g0)
    c: Horizontal(g2)
    c: Vertical(g1)
    c: Vertical(g3)
    c: DistanceY(g1,g1) = 23
    c: DistanceX(g0,g0) = 42
    c: DistanceY(g-1,g0) = 12
    c: Distance(g0,g-3) = 1
FEATURE [PartDesign::Pocket] Pocket012
  AllowMultiFace = false
  BaseFeature = -> Fillet006
  Length = 1.5
  Length2 = 100
  Profile = -> Sketch024
  Type = 0
FEATURE [Sketcher::SketchObject] Sketch026
  FullyConstrained = true
  MapMode = 5
  Support = -> [XY_Plane001]
  sketch-geometry (16):
    g0: LineSegment StartX=-47 StartY=20 StartZ=0 EndX=47 EndY=20 EndZ=0
    g1: LineSegment StartX=47 StartY=20 StartZ=0 EndX=47 EndY=-20 EndZ=0
    g2: LineSegment StartX=47 StartY=-20 StartZ=0 EndX=-47 EndY=-20 EndZ=0
    g3: LineSegment StartX=-47 StartY=-20 StartZ=0 EndX=-47 EndY=20 EndZ=0
    g4: Circle CenterX=-42.85 CenterY=15 CenterZ=0 NormalX=0 NormalY=0 NormalZ=1 AngleXU=0 Radius=1.5
    g5: Circle CenterX=-42.85 CenterY=-15 CenterZ=0 NormalX=0 NormalY=0 NormalZ=1 AngleXU=0 Radius=1.5
    g6: Circle CenterX=42.85 CenterY=15 CenterZ=0 NormalX=0 NormalY=0 NormalZ=1 AngleXU=0 Radius=1.5
    g7: Circle CenterX=42.85 CenterY=-15 CenterZ=0 NormalX=0 NormalY=0 NormalZ=1 AngleXU=0 Radius=1.5
    g8: LineSegment StartX=-32.25 StartY=15.5 StartZ=0 EndX=37.75 EndY=15.5 EndZ=0
    g9: LineSegment StartX=37.75 StartY=15.5 StartZ=0 EndX=37.75 EndY=-15.5 EndZ=0
    g10: LineSegment StartX=37.75 StartY=-15.5 StartZ=0 EndX=-32.25 EndY=-15.5 EndZ=0
    g11: LineSegment StartX=-32.25 StartY=-15.5 StartZ=0 EndX=-32.25 EndY=15.5 EndZ=0
    g12: LineSegment StartX=-39.75 StartY=18.75 StartZ=0 EndX=39.75 EndY=18.75 EndZ=0
    g13: LineSegment StartX=39.75 StartY=18.75 StartZ=0 EndX=39.75 EndY=-18.75 EndZ=0
    g14: LineSegment StartX=39.75 StartY=-18.75 StartZ=0 EndX=-39.75 EndY=-18.75 EndZ=0
    g15: LineSegment StartX=-39.75 StartY=-18.75 StartZ=0 EndX=-39.75 EndY=18.75 EndZ=0
  constraints (42):
    c: Coincident(g0,g1)
    c: Coincident(g1,g2)
    c: Coincident(g2,g3)
    c: Coincident(g3,g0)
    c: Horizontal(g0)
    c: Horizontal(g2)
    c: Vertical(g1)
    c: Vertical(g3)
    c: Symmetric(g1,g0,g-1)
    c: DistanceX(g0,g0) = 94
    c: DistanceY(g3,g3) = 40
    c: Radius(g4) = 1.5
    c: Equal(g4,g6)
    c: Equal(g4,g5)
    c: Equal(g4,g7)
    c: Symmetric(g5,g4,g-1)
    c: Symmetric(g6,g7,g-1)
    c: Symmetric(g4,g6,g-2)
    c: DistanceY(g-1,g4) = 15
    c: DistanceX(g-2,g4) = -42.85
    c: Coincident(g8,g9)
    c: Coincident(g9,g10)
    c: Coincident(g10,g11)
    c: Coincident(g11,g8)
    c: Horizontal(g8)
    c: Horizontal(g10)
    c: Vertical(g11)
    c: DistanceY(g9,g9) = 31
    c: DistanceX(g8,g8) = 70
    c: Symmetric(g8,g9,g-1)
    c: Coincident(g12,g13)
    c: Coincident(g13,g14)
    c: Coincident(g14,g15)
    c: Coincident(g15,g12)
    c: Horizontal(g12)
    c: Horizontal(g14)
    c: Vertical(g13)
    c: Vertical(g15)
    c: DistanceX(g12,g12) = 79.5
    c: Symmetric(g12,g13,g-1)
    c: DistanceY(g15,g15) = 37.5
    c: Distance(g8,g13) = 2
FEATURE [PartDesign::Pad] Pad009
  AllowMultiFace = false
  Direction = (1,1,1)
  Length = 3
  Length2 = 100
  Profile = -> Sketch026
  Type = 0
FEATURE [Sketcher::SketchObject] Sketch023
  FullyConstrained = true
  MapMode = 5
  Placement = pos=(0,0,0) rot=(1,0,0;3.14159rad)
  Support = -> [Pad009]
  sketch-geometry (4):
    g0: LineSegment StartX=-39.75 StartY=18.75 StartZ=0 EndX=39.75 EndY=18.75 EndZ=0
    g1: LineSegment StartX=39.75 StartY=18.75 StartZ=0 EndX=39.75 EndY=-18.75 EndZ=0
    g2: LineSegment StartX=39.75 StartY=-18.75 StartZ=0 EndX=-39.75 EndY=-18.75 EndZ=0
    g3: LineSegment StartX=-39.75 StartY=-18.75 StartZ=0 EndX=-39.75 EndY=18.75 EndZ=0
  constraints (11):
    c: Coincident(g0,g1)
    c: Coincident(g1,g2)
    c: Coincident(g2,g3)
    c: Coincident(g3,g0)
    c: Horizontal(g0)
    c: Horizontal(g2)
    c: Vertical(g1)
    c: Vertical(g3)
    c: DistanceY(g1,g1) = 37.5
    c: DistanceX(g0,g0) = 79.5
    c: Symmetric(g0,g2,g-1)
FEATURE [PartDesign::Pocket] Pocket011
  AllowMultiFace = false
  BaseFeature = -> Pad009
  Length = 1.5
  Length2 = 100
  Profile = -> Sketch023
  Type = 0
FEATURE [PartDesign::Fillet] Fillet005
  Base = -> Pocket011 [Edge5,Edge1,Edge8,Edge2]
  BaseFeature = -> Pocket011
  Radius = 5
  SupportTransform = false
FEATURE [PartDesign::Chamfer] Chamfer003
  Angle = 45
  Base = -> Fillet005 [Edge33,Edge34,Edge35,Edge36]
  BaseFeature = -> Fillet005
  ChamferType = 0
  FlipDirection = false
  Size = 2
  Size2 = 1
  SupportTransform = false
FEATURE [PartDesign::Body] Body001  label="Devant"
  Group = -> [Sketch026,Pad009,Sketch023,Pocket011,Fillet005,Chamfer003]
  Origin = -> Origin001
  Placement = pos=(12,-3.4e-15,77) rot=(-0.707107,0,-0.707107;3.14159rad)
  Tip = -> Chamfer003
FEATURE [Sketcher::SketchObject] Sketch030
  ExternalGeometry = -> [Pocket012]
  FullyConstrained = true
  MapMode = 5
  Placement = pos=(0,0,0) rot=(1,0,0;3.14159rad)
  Support = -> [Pocket012]
  sketch-geometry (12):
    g0: LineSegment StartX=-38.75 StartY=12 StartZ=0 EndX=3.25 EndY=12 EndZ=0
    g1: LineSegment StartX=3.25 StartY=12 StartZ=0 EndX=3.25 EndY=17 EndZ=0
    g2: LineSegment StartX=3.25 StartY=17 StartZ=0 EndX=-38.75 EndY=17 EndZ=0
    g3: LineSegment StartX=-38.75 StartY=17 StartZ=0 EndX=-38.75 EndY=12 EndZ=0
    g4: LineSegment StartX=-38.75 StartY=-11 StartZ=0 EndX=3.25 EndY=-11 EndZ=0
    g5: LineSegment StartX=3.25 StartY=-11 StartZ=0 EndX=3.25 EndY=-16 EndZ=0
    g6: LineSegment StartX=3.25 StartY=-16 StartZ=0 EndX=-38.75 EndY=-16 EndZ=0
    g7: LineSegment StartX=-38.75 StartY=-16 StartZ=0 EndX=-38.75 EndY=-11 EndZ=0
    g8: Circle CenterX=-26.25 CenterY=14.5 CenterZ=0 NormalX=0 NormalY=0 NormalZ=1 AngleXU=0 Radius=1.5
    g9: Circle CenterX=-26.25 CenterY=-13.5 CenterZ=0 NormalX=0 NormalY=0 NormalZ=1 AngleXU=0 Radius=1.5
    g10: Circle CenterX=-9.25 CenterY=14.5 CenterZ=0 NormalX=0 NormalY=0 NormalZ=1 AngleXU=0 Radius=1.5
    g11: Circle CenterX=-9.25 CenterY=-13.5 CenterZ=0 NormalX=0 NormalY=0 NormalZ=1 AngleXU=0 Radius=1.5
  constraints (32):
    c: Coincident(g0,g1)
    c: Coincident(g1,g2)
    c: Coincident(g2,g3)
    c: Coincident(g3,g0)
    c: Horizontal(g2)
    c: Vertical(g1)
    c: Vertical(g3)
    c: Coincident(g0,g-3)
    c: Coincident(g4,g5)
    c: Coincident(g5,g6)
    c: Coincident(g6,g7)
    c: Coincident(g7,g4)
    c: Horizontal(g6)
    c: Vertical(g5)
    c: Vertical(g7)
    c: Coincident(g4,g-4)
    c: Coincident(g4,g-4)
    c: Coincident(g0,g-3)
    c: Equal(g1,g5)
    c: DistanceY(g1,g1) = 5
    c: Radius(g11) = 1.5
    c: Equal(g11,g10)
    c: Equal(g11,g8)
    c: Equal(g11,g9)
    c: Distance(g8,g0) = 2.5
    c: Distance(g10,g0) = 2.5
    c: Distance(g8,g3) = 12.5
    c: Distance(g10,g1) = 12.5
    c: Distance(g9,g4) = 2.5
    c: Distance(g11,g4) = 2.5
    c: Distance(g9,g7) = 12.5
    c: Distance(g11,g5) = 12.5
FEATURE [PartDesign::Pad] Pad008
  BaseFeature = -> Pocket012
  Direction = (1,1,1)
  Length = 5
  Length2 = 100
  Profile = -> Sketch030
  Type = 0
FEATURE [PartDesign::Fillet] Fillet008
  Base = -> Pad008 [Edge55,Edge68,Edge58,Edge66]
  BaseFeature = -> Pad008
  Radius = 4
  SupportTransform = false
FEATURE [PartDesign::Body] Body006  label="Plaque"
  Group = -> [Sketch025,Pad011,Fillet006,Sketch024,Pocket012,Sketch030,Pad008,Fillet008]
  Origin = -> Origin008
  Placement = pos=(10,-3e-15,77) rot=(0.707107,0,0.707107;3.14159rad)
  Tip = -> Fillet008
FEATURE [Sketcher::SketchObject] Sketch034
  FullyConstrained = true
  MapMode = 5
  Placement = pos=(0,0,0) rot=(0.57735,0.57735,0.57735;2.0944rad)
  Support = -> [YZ_Plane009]
  sketch-geometry (24):
    g0: LineSegment StartX=-27.5 StartY=127.5 StartZ=0 EndX=27.5 EndY=127.5 EndZ=0
    g1: LineSegment StartX=-27.5 StartY=127.5 StartZ=0 EndX=-27.5 EndY=119.5 EndZ=0
    g2: LineSegment StartX=-27.5 StartY=119.5 StartZ=0 EndX=-22.5 EndY=119.5 EndZ=0
    g3: LineSegment StartX=-22.5 StartY=119.5 StartZ=0 EndX=-22.5 EndY=34.5 EndZ=0
    g4: LineSegment StartX=22.5 StartY=34.5 StartZ=0 EndX=22.5 EndY=119.5 EndZ=0
    g5: LineSegment StartX=22.5 StartY=119.5 StartZ=0 EndX=27.5 EndY=119.5 EndZ=0
    g6: LineSegment StartX=27.5 StartY=119.5 StartZ=0 EndX=27.5 EndY=127.5 EndZ=0
    g7: Circle CenterX=-23 CenterY=123.5 CenterZ=0 NormalX=0 NormalY=0 NormalZ=1 AngleXU=0 Radius=1.5
    g8: Circle CenterX=-15 CenterY=119.85 CenterZ=0 NormalX=0 NormalY=0 NormalZ=1 AngleXU=0 Radius=1.5
    g9: Circle CenterX=15 CenterY=119.85 CenterZ=0 NormalX=0 NormalY=0 NormalZ=1 AngleXU=0 Radius=1.5
    g10: Circle CenterX=23 CenterY=123.5 CenterZ=0 NormalX=0 NormalY=0 NormalZ=1 AngleXU=0 Radius=1.5
    g11: Circle CenterX=-23 CenterY=30.5 CenterZ=0 NormalX=0 NormalY=0 NormalZ=1 AngleXU=0 Radius=1.5
    g12: Circle CenterX=-15 CenterY=34.15 CenterZ=0 NormalX=0 NormalY=0 NormalZ=1 AngleXU=0 Radius=1.5
    g13: Circle CenterX=15 CenterY=34.15 CenterZ=0 NormalX=0 NormalY=0 NormalZ=1 AngleXU=0 Radius=1.5
    g14: Circle CenterX=23 CenterY=30.5 CenterZ=0 NormalX=0 NormalY=0 NormalZ=1 AngleXU=0 Radius=1.5
    g15: LineSegment StartX=22.5 StartY=34.5 StartZ=0 EndX=27.5 EndY=34.5 EndZ=0
    g16: LineSegment StartX=27.5 StartY=34.5 StartZ=0 EndX=34 EndY=4 EndZ=0
    g17: LineSegment StartX=34 StartY=4 StartZ=0 EndX=25.8203 EndY=4 EndZ=0
    g18: LineSegment StartX=25.8203 StartY=4 StartZ=0 EndX=21.0253 EndY=26.5 EndZ=0
    g19: LineSegment StartX=21.0253 StartY=26.5 StartZ=0 EndX=-21.0253 EndY=26.5 EndZ=0
    g20: LineSegment StartX=-21.0253 StartY=26.5 StartZ=0 EndX=-25.8203 EndY=4 EndZ=0
    g21: LineSegment StartX=-25.8203 StartY=4 StartZ=0 EndX=-34 EndY=4 EndZ=0
    g22: LineSegment StartX=-34 StartY=4 StartZ=0 EndX=-27.5 EndY=34.5 EndZ=0
    g23: LineSegment StartX=-27.5 StartY=34.5 StartZ=0 EndX=-22.5 EndY=34.5 EndZ=0
  constraints (59):
    c: Coincident(g0,g1)
    c: Vertical(g1)
    c: Coincident(g1,g2)
    c: Horizontal(g2)
    c: Coincident(g2,g3)
    c: Vertical(g3)
    c: Vertical(g4)
    c: Coincident(g4,g5)
    c: Horizontal(g5)
    c: Coincident(g5,g6)
    c: Coincident(g6,g0)
    c: Vertical(g6)
    c: Symmetric(g0,g0,g-2)
    c: Radius(g14) = 1.5
    c: Equal(g14,g13)
    c: Equal(g14,g12)
    c: Equal(g14,g11)
    c: Equal(g14, g7-g10) x4
    c: Symmetric(g7,g10,g-2)
    c: Symmetric(g8,g9,g-2)
    c: Symmetric(g12,g13,g-2)
    c: Symmetric(g11,g14,g-2)
    c: Distance(g12,g13) = 30
    c: Distance(g8,g9) = 30
    c: Distance(g8,g0) = 7.65
    c: Distance(g7,g0) = 4
    c: DistanceX(g-2,g7) = -23
    c: DistanceX(g-2,g11) = -23
    c: DistanceY(g6,g6) = 8
    c: DistanceY(g-1,g12) = 34.15
    c: DistanceY(g-1,g11) = 30.5
    c: Symmetric(g2,g4,g-2)
    c: DistanceX(g0,g0) = 55
    c: Coincident(g4,g15)
    c: Horizontal(g15)
    c: Coincident(g15,g16)
    c: Coincident(g16,g17)
    c: Coincident(g17,g18)
    c: Coincident(g18,g19)
    c: Coincident(g19,g20)
    c: Coincident(g20,g21)
    c: Coincident(g21,g22)
    c: Coincident(g22,g23)
    c: Coincident(g23,g3)
    c: Horizontal(g23)
    c: Symmetric(g22,g15,g-2)
    c: Symmetric(g19,g18,g-2)
    c: DistanceX(g2,g2) = 5
    c: Equal(g2,g23)
    c: Distance(g11,g19) = 4
    c: Distance(g3,g19) = 8
    c: DistanceY(g-1,g0) = 127.5
    c: Distance(g19,g22) = 8
    c: Horizontal(g17)
    c: DistanceY(g-1,g16) = 4
    c: Parallel(g18,g16)
    c: DistanceX(g-2,g16) = 34
    c: Symmetric(g21,g16,g-2)
    c: Symmetric(g20,g17,g-2)
FEATURE [PartDesign::Pad] Pad014
  Direction = (1,1,1)
  Length = 4
  Length2 = 100
  Placement = pos=(0,0,0) rot=(0.57735,0.57735,0.57735;2.0944rad)
  Profile = -> Sketch034
  Type = 0
FEATURE [Sketcher::SketchObject] Sketch035
  FullyConstrained = false
  MapMode = 5
  Support = -> [Pad014]
  sketch-geometry (8):
    g0: LineSegment StartX=17.5 StartY=-37.65 StartZ=0 EndX=17.5 EndY=-114.85 EndZ=0
    g1: LineSegment StartX=17.5 StartY=-114.85 StartZ=0 EndX=-17.5 EndY=-114.85 EndZ=0
    g2: LineSegment StartX=-17.5 StartY=-114.85 StartZ=0 EndX=-17.5 EndY=-37.65 EndZ=0
    g3: LineSegment StartX=-17.5 StartY=-37.65 StartZ=0 EndX=-12 EndY=-37.65 EndZ=0
    g4: LineSegment StartX=-12 StartY=-37.65 StartZ=0 EndX=-12 EndY=-17.65 EndZ=0
    g5: LineSegment StartX=-12 StartY=-17.65 StartZ=0 EndX=12 EndY=-17.65 EndZ=0
    g6: LineSegment StartX=12 StartY=-17.65 StartZ=0 EndX=12 EndY=-37.65 EndZ=0
    g7: LineSegment StartX=12 StartY=-37.65 StartZ=0 EndX=17.5 EndY=-37.65 EndZ=0
  constraints (17):
    c: Coincident(g0,g1)
    c: Coincident(g1,g2)
    c: Vertical(g0)
    c: Symmetric(g0,g1,g-2)
    c: Coincident(g2,g3)
    c: Horizontal(g3)
    c: Coincident(g3,g4)
    c: Vertical(g4)
    c: Coincident(g4,g5)
    c: Horizontal(g5)
    c: Coincident(g5,g6)
    c: Vertical(g6)
    c: Coincident(g6,g7)
    c: Coincident(g7,g0)
    c: Symmetric(g2,g0,g-2)
    c: Symmetric(g6,g3,g-2)
    c: DistanceY(g6,g6) = 20
FEATURE [PartDesign::Pocket] Pocket016
  BaseFeature = -> Pad014
  Length = 13
  Length2 = 100
  Placement = pos=(0,0,0) rot=(0.57735,0.57735,0.57735;2.0944rad)
  Profile = -> Sketch035
  Type = 0
FEATURE [Sketcher::SketchObject] Sketch036
  FullyConstrained = false
  MapMode = 5
  Support = -> [Pocket016]
  sketch-geometry (2):
    g0: Circle CenterX=-29 CenterY=-8 CenterZ=0 NormalX=0 NormalY=0 NormalZ=1 AngleXU=0 Radius=1.5
    g1: Circle CenterX=29 CenterY=-8 CenterZ=0 NormalX=0 NormalY=0 NormalZ=1 AngleXU=0 Radius=1.5
  constraints (4):
    c: Radius(g1) = 1.5
    c: Equal(g1,g0)
    c: Symmetric(g1,g0,g-2)
    c: DistanceX(g-2,g1) = 29
FEATURE [PartDesign::Pocket] Pocket017
  BaseFeature = -> Pocket016
  Length = 13
  Length2 = 100
  Placement = pos=(0,0,0) rot=(0.57735,0.57735,0.57735;2.0944rad)
  Profile = -> Sketch036
  Type = 0
FEATURE [PartDesign::Fillet] Fillet012
  Base = -> Pocket017 [Edge84,Edge78,Edge76,Edge73,Edge2,Edge75,Edge92,Edge79]
  BaseFeature = -> Pocket017
  Placement = pos=(0,0,0) rot=(0.57735,0.57735,0.57735;2.0944rad)
  Radius = 3
  SupportTransform = false
FEATURE [PartDesign::Fillet] Fillet013
  Base = -> Fillet012 [Edge115,Edge93]
  BaseFeature = -> Fillet012
  Placement = pos=(0,0,0) rot=(0.57735,0.57735,0.57735;2.0944rad)
  Radius = 3
  SupportTransform = false
FEATURE [PartDesign::Chamfer] Chamfer004
  Angle = 45
  Base = -> Fillet013 [Edge120,Edge132]
  BaseFeature = -> Fillet013
  ChamferType = 0
  FlipDirection = false
  Placement = pos=(0,0,0) rot=(0.57735,0.57735,0.57735;2.0944rad)
  Size = 1.5
  Size2 = 1
  SupportTransform = false
FEATURE [PartDesign::Body] Body009  label="support_plaque_ecran"
  Group = -> [Sketch034,Pad014,Sketch035,Pocket016,Sketch036,Pocket017,Fillet012,Fillet013,Chamfer004]
  Origin = -> Origin010
  Placement = pos=(6,0,0) rot=(0,0,1;0rad)
  Tip = -> Chamfer004
FEATURE [Mesh::Feature] Mesh002  label="support_plaque_ecran (Meshed)"
FEATURE [Sketcher::SketchObject] Sketch037
  ExternalGeometry = -> [Pad003]
  FullyConstrained = true
  MapMode = 5
  Placement = pos=(0,0,4) rot=(0,0,1;0rad)
  Support = -> [Pad003]
  sketch-geometry (8):
    g0: LineSegment StartX=0 StartY=35.4965 StartZ=0 EndX=6 EndY=35.4965 EndZ=0
    g1: LineSegment StartX=6 StartY=35.4965 StartZ=0 EndX=6 EndY=23.4965 EndZ=0
    g2: LineSegment StartX=6 StartY=23.4965 StartZ=0 EndX=0 EndY=23.4965 EndZ=0
    g3: LineSegment StartX=0 StartY=23.4965 StartZ=0 EndX=0 EndY=35.4965 EndZ=0
    g4: LineSegment StartX=0 StartY=-24 StartZ=0 EndX=6 EndY=-24 EndZ=0
    g5: LineSegment StartX=6 StartY=-24 StartZ=0 EndX=6 EndY=-36 EndZ=0
    g6: LineSegment StartX=6 StartY=-36 StartZ=0 EndX=0 EndY=-36 EndZ=0
    g7: LineSegment StartX=0 StartY=-36 StartZ=0 EndX=0 EndY=-24 EndZ=0
  constraints (24):
    c: Coincident(g0,g1)
    c: Coincident(g1,g2)
    c: Coincident(g2,g3)
    c: Coincident(g3,g0)
    c: Horizontal(g0)
    c: Horizontal(g2)
    c: Vertical(g1)
    c: Vertical(g3)
    c: Coincident(g4,g5)
    c: Coincident(g5,g6)
    c: Coincident(g6,g7)
    c: Coincident(g7,g4)
    c: Horizontal(g4)
    c: Horizontal(g6)
    c: Vertical(g5)
    c: Vertical(g7)
    c: PointOnObject(g0,g-2)
    c: DistanceX(g4,g4) = 6
    c: DistanceX(g2,g2) = 6
    c: DistanceY(g3,g3) = 12
    c: DistanceY(g7,g7) = 12
    c: PointOnObject(g0,g-4)
    c: PointOnObject(g4,g-2)
    c: PointOnObject(g6,g-4)
FEATURE [PartDesign::Pad] Pad015
  BaseFeature = -> Pad003
  Direction = (1,1,1)
  Length = 8
  Length2 = 100
  Profile = -> Sketch037
  Type = 0
FEATURE [Sketcher::SketchObject] Sketch038
  FullyConstrained = false
  MapMode = 5
  Support = -> [Pad015]
  sketch-geometry (15):
    g0: LineSegment StartX=35.4965 StartY=4 StartZ=0 EndX=34.0144 EndY=4 EndZ=0
    g1: LineSegment StartX=34.0144 StartY=4 StartZ=0 EndX=32.3432 EndY=12 EndZ=0
    g2: LineSegment StartX=32.3432 StartY=12 StartZ=0 EndX=35.4965 EndY=12 EndZ=0
    g3: LineSegment StartX=35.4965 StartY=12 StartZ=0 EndX=35.4965 EndY=4 EndZ=0
    g4: LineSegment StartX=23.4965 StartY=4 StartZ=0 EndX=25.8363 EndY=4 EndZ=0
    g5: LineSegment StartX=25.8363 StartY=4 StartZ=0 EndX=24.094 EndY=12 EndZ=0
    g6: LineSegment StartX=24.094 StartY=12 StartZ=0 EndX=23.4965 EndY=12 EndZ=0
    g7: LineSegment StartX=23.4965 StartY=12 StartZ=0 EndX=23.4965 EndY=4 EndZ=0
    g8: LineSegment StartX=-24 StartY=4 StartZ=0 EndX=-25.7965 EndY=4 EndZ=0
    g9: LineSegment StartX=-25.7965 StartY=4 StartZ=0 EndX=-24 EndY=12 EndZ=0
    g10: LineSegment StartX=-24 StartY=12 StartZ=0 EndX=-24 EndY=4 EndZ=0
    g11: LineSegment StartX=-36 StartY=4 StartZ=0 EndX=-34.0101 EndY=4 EndZ=0
    g12: LineSegment StartX=-34.0101 StartY=4 StartZ=0 EndX=-32.2323 EndY=12 EndZ=0
    g13: LineSegment StartX=-32.2323 StartY=12 StartZ=0 EndX=-36 EndY=12 EndZ=0
    g14: LineSegment StartX=-36 StartY=12 StartZ=0 EndX=-36 EndY=4 EndZ=0
  constraints (19):
    c: Horizontal(g0)
    c: Coincident(g0,g1)
    c: Coincident(g1,g2)
    c: Coincident(g2,g3)
    c: Coincident(g3,g0)
    c: Horizontal(g4)
    c: Coincident(g4,g5)
    c: Coincident(g5,g6)
    c: Coincident(g6,g7)
    c: Coincident(g7,g4)
    c: Horizontal(g8)
    c: Coincident(g8,g9)
    c: Coincident(g9,g10)
    c: Coincident(g10,g8)
    c: Horizontal(g11)
    c: Coincident(g11,g12)
    c: Coincident(g12,g13)
    c: Coincident(g13,g14)
    c: Coincident(g14,g11)
FEATURE [PartDesign::Pocket] Pocket018
  BaseFeature = -> Pad015
  Length = 8
  Length2 = 100
  Profile = -> Sketch038
  Type = 0
FEATURE [Sketcher::SketchObject] Sketch039
  FullyConstrained = true
  MapMode = 5
  Support = -> [Pocket018]
  sketch-geometry (2):
    g0: Circle CenterX=-29 CenterY=7.95 CenterZ=0 NormalX=0 NormalY=0 NormalZ=1 AngleXU=0 Radius=1.5
    g1: Circle CenterX=29 CenterY=7.95 CenterZ=0 NormalX=0 NormalY=0 NormalZ=1 AngleXU=0 Radius=1.5
  constraints (5):
    c: Radius(g1) = 1.5
    c: Equal(g1,g0)
    c: Symmetric(g0,g1,g-2)
    c: DistanceX(g-2,g0) = -29
    c: DistanceY(g-1,g0) = 7.95
FEATURE [PartDesign::Pocket] Pocket019
  BaseFeature = -> Pocket018
  Length = 9
  Length2 = 100
  Profile = -> Sketch039
  Type = 0
FEATURE [PartDesign::Body] Body005  label="fixation_support_plaque_ecran"
  Group = -> [Sketch019,Pad003,Sketch037,Pad015,Sketch038,Pocket018,Sketch039,Pocket019]
  Origin = -> Origin005
  Tip = -> Pocket019
FEATURE [App::MeasureDistance] Distance  label="Distance: 19.76 mm"
  Distance = 19.7627
  P1 = (-15.2125,25.8857,88.3136)
  P2 = (1.05463e-05,38.5,88.4688)
FEATURE [Sketcher::SketchObject] Sketch040
  FullyConstrained = true
  MapMode = 5
  Support = -> [XY_Plane010]
  sketch-geometry (15):
    g0: LineSegment StartX=0 StartY=-17.91 StartZ=0 EndX=0 EndY=-26.91 EndZ=0
    g1: LineSegment StartX=0 StartY=-26.91 StartZ=0 EndX=0 EndY=-31.91 EndZ=0
    g2: LineSegment StartX=0 StartY=-31.91 StartZ=0 EndX=5 EndY=-31.91 EndZ=0
    g3: LineSegment StartX=5 StartY=-31.91 StartZ=0 EndX=5 EndY=-29.91 EndZ=0
    g4: LineSegment StartX=5 StartY=-29.91 StartZ=0 EndX=2 EndY=-29.91 EndZ=0
    g5: LineSegment StartX=2 StartY=-29.91 StartZ=0 EndX=2 EndY=-26.91 EndZ=0
    g6: LineSegment StartX=2 StartY=-26.91 StartZ=0 EndX=16 EndY=-26.91 EndZ=0
    g7: LineSegment StartX=16 StartY=-26.91 StartZ=0 EndX=16 EndY=-29.91 EndZ=0
    g8: LineSegment StartX=16 StartY=-29.91 StartZ=0 EndX=13 EndY=-29.91 EndZ=0
    g9: LineSegment StartX=13 StartY=-29.91 StartZ=0 EndX=13 EndY=-31.91 EndZ=0
    g10: LineSegment StartX=13 StartY=-31.91 StartZ=0 EndX=18 EndY=-31.91 EndZ=0
    g11: LineSegment StartX=18 StartY=-31.91 StartZ=0 EndX=18 EndY=-24.91 EndZ=0
    g12: LineSegment StartX=18 StartY=-24.91 StartZ=0 EndX=2 EndY=-24.91 EndZ=0
    g13: LineSegment StartX=2 StartY=-24.91 StartZ=0 EndX=2 EndY=-17.91 EndZ=0
    g14: LineSegment StartX=2 StartY=-17.91 StartZ=0 EndX=0 EndY=-17.91 EndZ=0
  constraints (45):
    c: Vertical(g1)
    c: Coincident(g1,g2)
    c: Horizontal(g2)
    c: Coincident(g2,g3)
    c: Vertical(g3)
    c: Coincident(g3,g4)
    c: Horizontal(g4)
    c: Coincident(g4,g5)
    c: Coincident(g5,g6)
    c: Horizontal(g6)
    c: Coincident(g6,g7)
    c: Vertical(g7)
    c: Coincident(g7,g8)
    c: Horizontal(g8)
    c: Coincident(g8,g9)
    c: Vertical(g9)
    c: Coincident(g9,g10)
    c: Horizontal(g10)
    c: Coincident(g10,g11)
    c: Vertical(g11)
    c: Coincident(g11,g12)
    c: Horizontal(g12)
    c: Coincident(g12,g13)
    c: Vertical(g13)
    c: Coincident(g13,g14)
    c: Coincident(g14,g0)
    c: Horizontal(g14)
    c: DistanceX(g6,g6) = 14
    c: DistanceY(g5,g5) = 3
    c: DistanceY(g7,g7) = 3
    c: Distance(g4,g1) = 2
    c: Distance(g6,g12) = 2
    c: Distance(g7,g11) = 2
    c: Distance(g3,g2) = 2
    c: Distance(g8,g10) = 2
    c: DistanceX(g4,g4) = 3
    c: DistanceX(g8,g8) = 3
    c: Vertical(g0)
    c: DistanceX(g14,g14) = 2
    c: DistanceY(g0,g0) = 9
    c: Vertical(g5)
    c: PointOnObject(g1,g-2)
    c: DistanceY(g-1,g0) = -26.91
    c: Coincident(g0,g1)
    c: DistanceY(g13,g13) = 7
FEATURE [PartDesign::Pad] Pad016
  Direction = (1,1,1)
  Length = 9
  Length2 = 100
  Profile = -> Sketch040
  Type = 0
FEATURE [Sketcher::SketchObject] Sketch041
  FullyConstrained = false
  MapMode = 5
  Support = -> [Pad016]
  sketch-geometry (1):
    g0: Circle CenterX=-21.91 CenterY=4.5 CenterZ=0 NormalX=0 NormalY=0 NormalZ=1 AngleXU=0 Radius=1.75
  constraints (2):
    c: DistanceY(g-1,g0) = 4.5
    c: Radius(g0) = 1.75
FEATURE [PartDesign::Pocket] Pocket020
  BaseFeature = -> Pad016
  Length = 12
  Length2 = 100
  Profile = -> Sketch041
  Type = 0
FEATURE [PartDesign::Fillet] Fillet014
  Base = -> Pocket020 [Edge7,Edge8]
  BaseFeature = -> Pocket020
  Radius = 4
  SupportTransform = false
FEATURE [PartDesign::Fillet] Fillet015
  Base = -> Fillet014 [Edge45,Edge50,Edge41,Edge48,Edge46]
  BaseFeature = -> Fillet014
  Radius = 1
  SupportTransform = false
FEATURE [PartDesign::Body] Body010  label="attache_leds"
  Group = -> [Sketch040,Pad016,Sketch041,Pocket020,Fillet014,Fillet015]
  Origin = -> Origin011
  Placement = pos=(6,-1,35) rot=(0,1,0;3.14159rad)
  Tip = -> Fillet015
FEATURE [Mesh::Feature] Mesh003  label="attache_leds (Meshed)"
FEATURE [Sketcher::SketchObject] Sketch042
  FullyConstrained = true
  MapMode = 5
  Support = -> [XY_Plane011]
  sketch-geometry (15):
    g0: LineSegment StartX=0 StartY=-17.91 StartZ=0 EndX=0 EndY=-26.91 EndZ=0
    g1: LineSegment StartX=0 StartY=-26.91 StartZ=0 EndX=0 EndY=-31.91 EndZ=0
    g2: LineSegment StartX=0 StartY=-31.91 StartZ=0 EndX=5 EndY=-31.91 EndZ=0
    g3: LineSegment StartX=5 StartY=-31.91 StartZ=0 EndX=5 EndY=-29.91 EndZ=0
    g4: LineSegment StartX=5 StartY=-29.91 StartZ=0 EndX=2 EndY=-29.91 EndZ=0
    g5: LineSegment StartX=2 StartY=-29.91 StartZ=0 EndX=2 EndY=-26.91 EndZ=0
    g6: LineSegment StartX=2 StartY=-26.91 StartZ=0 EndX=16 EndY=-26.91 EndZ=0
    g7: LineSegment StartX=16 StartY=-26.91 StartZ=0 EndX=16 EndY=-29.91 EndZ=0
    g8: LineSegment StartX=16 StartY=-29.91 StartZ=0 EndX=13 EndY=-29.91 EndZ=0
    g9: LineSegment StartX=13 StartY=-29.91 StartZ=0 EndX=13 EndY=-31.91 EndZ=0
    g10: LineSegment StartX=13 StartY=-31.91 StartZ=0 EndX=18 EndY=-31.91 EndZ=0
    g11: LineSegment StartX=18 StartY=-31.91 StartZ=0 EndX=18 EndY=-24.91 EndZ=0
    g12: LineSegment StartX=18 StartY=-24.91 StartZ=0 EndX=2 EndY=-24.91 EndZ=0
    g13: LineSegment StartX=2 StartY=-24.91 StartZ=0 EndX=2 EndY=-17.91 EndZ=0
    g14: LineSegment StartX=2 StartY=-17.91 StartZ=0 EndX=0 EndY=-17.91 EndZ=0
  constraints (45):
    c: Vertical(g1)
    c: Coincident(g1,g2)
    c: Horizontal(g2)
    c: Coincident(g2,g3)
    c: Vertical(g3)
    c: Coincident(g3,g4)
    c: Horizontal(g4)
    c: Coincident(g4,g5)
    c: Coincident(g5,g6)
    c: Horizontal(g6)
    c: Coincident(g6,g7)
    c: Vertical(g7)
    c: Coincident(g7,g8)
    c: Horizontal(g8)
    c: Coincident(g8,g9)
    c: Vertical(g9)
    c: Coincident(g9,g10)
    c: Horizontal(g10)
    c: Coincident(g10,g11)
    c: Vertical(g11)
    c: Coincident(g11,g12)
    c: Horizontal(g12)
    c: Coincident(g12,g13)
    c: Vertical(g13)
    c: Coincident(g13,g14)
    c: Coincident(g14,g0)
    c: Horizontal(g14)
    c: DistanceX(g6,g6) = 14
    c: DistanceY(g5,g5) = 3
    c: DistanceY(g7,g7) = 3
    c: Distance(g4,g1) = 2
    c: Distance(g6,g12) = 2
    c: Distance(g7,g11) = 2
    c: Distance(g3,g2) = 2
    c: Distance(g8,g10) = 2
    c: DistanceX(g4,g4) = 3
    c: DistanceX(g8,g8) = 3
    c: Vertical(g0)
    c: DistanceX(g14,g14) = 2
    c: DistanceY(g0,g0) = 9
    c: Vertical(g5)
    c: PointOnObject(g1,g-2)
    c: DistanceY(g-1,g0) = -26.91
    c: Coincident(g0,g1)
    c: DistanceY(g13,g13) = 7
FEATURE [PartDesign::Pad] Pad017
  Direction = (1,1,1)
  Length = 9
  Length2 = 100
  Profile = -> Sketch042
  Type = 0
FEATURE [Sketcher::SketchObject] Sketch043
  FullyConstrained = false
  MapMode = 5
  Support = -> [Pad017]
  sketch-geometry (1):
    g0: Circle CenterX=-21.91 CenterY=4.5 CenterZ=0 NormalX=0 NormalY=0 NormalZ=1 AngleXU=0 Radius=1.75
  constraints (2):
    c: DistanceY(g-1,g0) = 4.5
    c: Radius(g0) = 1.75
FEATURE [PartDesign::Pocket] Pocket021
  BaseFeature = -> Pad017
  Length = 12
  Length2 = 100
  Profile = -> Sketch043
  Type = 0
FEATURE [PartDesign::Fillet] Fillet016
  Base = -> Pocket021 [Edge7,Edge8]
  BaseFeature = -> Pocket021
  Radius = 4
  SupportTransform = false
FEATURE [PartDesign::Fillet] Fillet017
  Base = -> Fillet016 [Edge45,Edge50,Edge41,Edge48,Edge46]
  BaseFeature = -> Fillet016
  Radius = 1
  SupportTransform = false
FEATURE [PartDesign::Body] Body011  label="attache_leds001"
  Group = -> [Sketch042,Pad017,Sketch043,Pocket021,Fillet016,Fillet017]
  Origin = -> Origin012
  Placement = pos=(6,-1,128) rot=(0,1,0;3.14159rad)
  Tip = -> Fillet017
FEATURE [Sketcher::SketchObject] Sketch045
  FullyConstrained = true
  MapMode = 5
  Support = -> [XY_Plane012]
  sketch-geometry (15):
    g0: LineSegment StartX=0 StartY=-17.91 StartZ=0 EndX=0 EndY=-26.91 EndZ=0
    g1: LineSegment StartX=0 StartY=-26.91 StartZ=0 EndX=0 EndY=-31.91 EndZ=0
    g2: LineSegment StartX=0 StartY=-31.91 StartZ=0 EndX=5 EndY=-31.91 EndZ=0
    g3: LineSegment StartX=5 StartY=-31.91 StartZ=0 EndX=5 EndY=-29.91 EndZ=0
    g4: LineSegment StartX=5 StartY=-29.91 StartZ=0 EndX=2 EndY=-29.91 EndZ=0
    g5: LineSegment StartX=2 StartY=-29.91 StartZ=0 EndX=2 EndY=-26.91 EndZ=0
    g6: LineSegment StartX=2 StartY=-26.91 StartZ=0 EndX=16 EndY=-26.91 EndZ=0
    g7: LineSegment StartX=16 StartY=-26.91 StartZ=0 EndX=16 EndY=-29.91 EndZ=0
    g8: LineSegment StartX=16 StartY=-29.91 StartZ=0 EndX=13 EndY=-29.91 EndZ=0
    g9: LineSegment StartX=13 StartY=-29.91 StartZ=0 EndX=13 EndY=-31.91 EndZ=0
    g10: LineSegment StartX=13 StartY=-31.91 StartZ=0 EndX=18 EndY=-31.91 EndZ=0
    g11: LineSegment StartX=18 StartY=-31.91 StartZ=0 EndX=18 EndY=-24.91 EndZ=0
    g12: LineSegment StartX=18 StartY=-24.91 StartZ=0 EndX=2 EndY=-24.91 EndZ=0
    g13: LineSegment StartX=2 StartY=-24.91 StartZ=0 EndX=2 EndY=-17.91 EndZ=0
    g14: LineSegment StartX=2 StartY=-17.91 StartZ=0 EndX=0 EndY=-17.91 EndZ=0
  constraints (45):
    c: Vertical(g1)
    c: Coincident(g1,g2)
    c: Horizontal(g2)
    c: Coincident(g2,g3)
    c: Vertical(g3)
    c: Coincident(g3,g4)
    c: Horizontal(g4)
    c: Coincident(g4,g5)
    c: Coincident(g5,g6)
    c: Horizontal(g6)
    c: Coincident(g6,g7)
    c: Vertical(g7)
    c: Coincident(g7,g8)
    c: Horizontal(g8)
    c: Coincident(g8,g9)
    c: Vertical(g9)
    c: Coincident(g9,g10)
    c: Horizontal(g10)
    c: Coincident(g10,g11)
    c: Vertical(g11)
    c: Coincident(g11,g12)
    c: Horizontal(g12)
    c: Coincident(g12,g13)
    c: Vertical(g13)
    c: Coincident(g13,g14)
    c: Coincident(g14,g0)
    c: Horizontal(g14)
    c: DistanceX(g6,g6) = 14
    c: DistanceY(g5,g5) = 3
    c: DistanceY(g7,g7) = 3
    c: Distance(g4,g1) = 2
    c: Distance(g6,g12) = 2
    c: Distance(g7,g11) = 2
    c: Distance(g3,g2) = 2
    c: Distance(g8,g10) = 2
    c: DistanceX(g4,g4) = 3
    c: DistanceX(g8,g8) = 3
    c: Vertical(g0)
    c: DistanceX(g14,g14) = 2
    c: DistanceY(g0,g0) = 9
    c: Vertical(g5)
    c: PointOnObject(g1,g-2)
    c: DistanceY(g-1,g0) = -26.91
    c: Coincident(g0,g1)
    c: DistanceY(g13,g13) = 7
FEATURE [PartDesign::Pad] Pad018
  Direction = (1,1,1)
  Length = 9
  Length2 = 100
  Profile = -> Sketch045
  Type = 0
FEATURE [Sketcher::SketchObject] Sketch044
  FullyConstrained = false
  MapMode = 5
  Support = -> [Pad018]
  sketch-geometry (1):
    g0: Circle CenterX=-21.91 CenterY=4.5 CenterZ=0 NormalX=0 NormalY=0 NormalZ=1 AngleXU=0 Radius=1.75
  constraints (2):
    c: DistanceY(g-1,g0) = 4.5
    c: Radius(g0) = 1.75
FEATURE [PartDesign::Pocket] Pocket022
  BaseFeature = -> Pad018
  Length = 12
  Length2 = 100
  Profile = -> Sketch044
  Type = 0
FEATURE [PartDesign::Fillet] Fillet018
  Base = -> Pocket022 [Edge7,Edge8]
  BaseFeature = -> Pocket022
  Radius = 4
  SupportTransform = false
FEATURE [PartDesign::Fillet] Fillet019
  Base = -> Fillet018 [Edge45,Edge50,Edge41,Edge48,Edge46]
  BaseFeature = -> Fillet018
  Radius = 1
  SupportTransform = false
FEATURE [PartDesign::Body] Body012  label="attache_leds002"
  Group = -> [Sketch045,Pad018,Sketch044,Pocket022,Fillet018,Fillet019]
  Origin = -> Origin013
  Placement = pos=(6,1,119) rot=(0,0,-1;3.14159rad)
  Tip = -> Fillet019
FEATURE [Sketcher::SketchObject] Sketch046
  FullyConstrained = true
  MapMode = 5
  Support = -> [XY_Plane013]
  sketch-geometry (15):
    g0: LineSegment StartX=0 StartY=-17.91 StartZ=0 EndX=0 EndY=-26.91 EndZ=0
    g1: LineSegment StartX=0 StartY=-26.91 StartZ=0 EndX=0 EndY=-31.91 EndZ=0
    g2: LineSegment StartX=0 StartY=-31.91 StartZ=0 EndX=5 EndY=-31.91 EndZ=0
    g3: LineSegment StartX=5 StartY=-31.91 StartZ=0 EndX=5 EndY=-29.91 EndZ=0
    g4: LineSegment StartX=5 StartY=-29.91 StartZ=0 EndX=2 EndY=-29.91 EndZ=0
    g5: LineSegment StartX=2 StartY=-29.91 StartZ=0 EndX=2 EndY=-26.91 EndZ=0
    g6: LineSegment StartX=2 StartY=-26.91 StartZ=0 EndX=16 EndY=-26.91 EndZ=0
    g7: LineSegment StartX=16 StartY=-26.91 StartZ=0 EndX=16 EndY=-29.91 EndZ=0
    g8: LineSegment StartX=16 StartY=-29.91 StartZ=0 EndX=13 EndY=-29.91 EndZ=0
    g9: LineSegment StartX=13 StartY=-29.91 StartZ=0 EndX=13 EndY=-31.91 EndZ=0
    g10: LineSegment StartX=13 StartY=-31.91 StartZ=0 EndX=18 EndY=-31.91 EndZ=0
    g11: LineSegment StartX=18 StartY=-31.91 StartZ=0 EndX=18 EndY=-24.91 EndZ=0
    g12: LineSegment StartX=18 StartY=-24.91 StartZ=0 EndX=2 EndY=-24.91 EndZ=0
    g13: LineSegment StartX=2 StartY=-24.91 StartZ=0 EndX=2 EndY=-17.91 EndZ=0
    g14: LineSegment StartX=2 StartY=-17.91 StartZ=0 EndX=0 EndY=-17.91 EndZ=0
  constraints (45):
    c: Vertical(g1)
    c: Coincident(g1,g2)
    c: Horizontal(g2)
    c: Coincident(g2,g3)
    c: Vertical(g3)
    c: Coincident(g3,g4)
    c: Horizontal(g4)
    c: Coincident(g4,g5)
    c: Coincident(g5,g6)
    c: Horizontal(g6)
    c: Coincident(g6,g7)
    c: Vertical(g7)
    c: Coincident(g7,g8)
    c: Horizontal(g8)
    c: Coincident(g8,g9)
    c: Vertical(g9)
    c: Coincident(g9,g10)
    c: Horizontal(g10)
    c: Coincident(g10,g11)
    c: Vertical(g11)
    c: Coincident(g11,g12)
    c: Horizontal(g12)
    c: Coincident(g12,g13)
    c: Vertical(g13)
    c: Coincident(g13,g14)
    c: Coincident(g14,g0)
    c: Horizontal(g14)
    c: DistanceX(g6,g6) = 14
    c: DistanceY(g5,g5) = 3
    c: DistanceY(g7,g7) = 3
    c: Distance(g4,g1) = 2
    c: Distance(g6,g12) = 2
    c: Distance(g7,g11) = 2
    c: Distance(g3,g2) = 2
    c: Distance(g8,g10) = 2
    c: DistanceX(g4,g4) = 3
    c: DistanceX(g8,g8) = 3
    c: Vertical(g0)
    c: DistanceX(g14,g14) = 2
    c: DistanceY(g0,g0) = 9
    c: Vertical(g5)
    c: PointOnObject(g1,g-2)
    c: DistanceY(g-1,g0) = -26.91
    c: Coincident(g0,g1)
    c: DistanceY(g13,g13) = 7
FEATURE [PartDesign::Pad] Pad019
  Direction = (1,1,1)
  Length = 9
  Length2 = 100
  Profile = -> Sketch046
  Type = 0
FEATURE [Sketcher::SketchObject] Sketch047
  FullyConstrained = false
  MapMode = 5
  Support = -> [Pad019]
  sketch-geometry (1):
    g0: Circle CenterX=-21.91 CenterY=4.5 CenterZ=0 NormalX=0 NormalY=0 NormalZ=1 AngleXU=0 Radius=1.75
  constraints (2):
    c: DistanceY(g-1,g0) = 4.5
    c: Radius(g0) = 1.75
FEATURE [PartDesign::Pocket] Pocket023
  BaseFeature = -> Pad019
  Length = 12
  Length2 = 100
  Profile = -> Sketch047
  Type = 0
FEATURE [PartDesign::Fillet] Fillet020
  Base = -> Pocket023 [Edge7,Edge8]
  BaseFeature = -> Pocket023
  Radius = 4
  SupportTransform = false
FEATURE [PartDesign::Fillet] Fillet021
  Base = -> Fillet020 [Edge45,Edge50,Edge41,Edge48,Edge46]
  BaseFeature = -> Fillet020
  Radius = 1
  SupportTransform = false
FEATURE [PartDesign::Body] Body013  label="attache_leds003"
  Group = -> [Sketch046,Pad019,Sketch047,Pocket023,Fillet020,Fillet021]
  Origin = -> Origin014
  Placement = pos=(6,1,26) rot=(0,0,1;3.14159rad)
  Tip = -> Fillet021
FEATURE [Sketcher::SketchObject] Sketch048
  FullyConstrained = true
  MapMode = 5
  Placement = pos=(0,0,0) rot=(1,0,0;1.5708rad)
  Support = -> [XZ_Plane014]
  sketch-geometry (4):
    g0: LineSegment StartX=-340 StartY=330 StartZ=0 EndX=140 EndY=330 EndZ=0
    g1: LineSegment StartX=140 StartY=330 StartZ=0 EndX=140 EndY=-230 EndZ=0
    g2: LineSegment StartX=140 StartY=-230 StartZ=0 EndX=-340 EndY=-230 EndZ=0
    g3: LineSegment StartX=-340 StartY=-230 StartZ=0 EndX=-340 EndY=330 EndZ=0
  constraints (12):
    c: Coincident(g0,g1)
    c: Coincident(g1,g2)
    c: Coincident(g2,g3)
    c: Coincident(g3,g0)
    c: Horizontal(g0)
    c: Horizontal(g2)
    c: Vertical(g1)
    c: Vertical(g3)
    c: DistanceX(g0,g0) = 480
    c: DistanceY(g1,g1) = 560
    c: DistanceX(g-2,g0) = 140
    c: DistanceY(g-1,g1) = -230
FEATURE [PartDesign::Pad] Pad020
  Direction = (0,-1,2e-16)
  Length = 25
  Length2 = 100
  Placement = pos=(0,0,0) rot=(1,0,0;1.5708rad)
  Profile = -> Sketch048
  Type = 0
FEATURE [PartDesign::Fillet] Fillet022
  Base = -> Pad020 [Edge5,Edge2,Edge1,Edge8]
  BaseFeature = -> Pad020
  Placement = pos=(0,0,0) rot=(1,0,0;1.5708rad)
  Radius = 60
  SupportTransform = false
FEATURE [PartDesign::Body] Body014  label="base001"
  Group = -> [Sketch048,Pad020,Fillet022]
  Origin = -> Origin015
  Placement = pos=(0,85,0) rot=(0,0,1;0rad)
  Tip = -> Fillet022
FEATURE [Sketcher::SketchObject] Sketch050
  FullyConstrained = true
  MapMode = 5
  Support = -> [XY_Plane016]
  sketch-geometry (5):
    g0: LineSegment StartX=-70 StartY=60 StartZ=0 EndX=-70 EndY=-52 EndZ=0
    g1: LineSegment StartX=-70 StartY=-52 StartZ=0 EndX=143.261 EndY=-109.143 EndZ=0
    g2: LineSegment StartX=70 StartY=60 StartZ=0 EndX=-70 EndY=60 EndZ=0
    g3: Circle CenterX=0 CenterY=0 CenterZ=0 NormalX=0 NormalY=0 NormalZ=1 AngleXU=0 Radius=47.5
    g4: ArcOfCircle CenterX=0 CenterY=-70.7564 CenterZ=0 NormalX=0 NormalY=0 NormalZ=1 AngleXU=0 Radius=148.315 StartAngle=6.02139 EndAngle=7.36246
  constraints (14):
    c: Vertical(g0)
    c: Coincident(g0,g1)
    c: Coincident(g2,g0)
    c: Angle(g1,g-1) = 0.261799
    c: DistanceY(g-1,g2) = 60
    c: Coincident(g3,g-1)
    c: Radius(g3) = 47.5
    c: Symmetric(g0,g2,g-2)
    c: DistanceX(g2,g2) = 140
    c: DistanceY(g0,g0) = 112
    c: Coincident(g4,g2)
    c: Coincident(g4,g1)
    c: PointOnObject(g4,g-2)
    c: PointOnObject(g4,g1)
FEATURE [PartDesign::Pad] Pad022
  Direction = (0,0,1)
  Length = 10
  Length2 = 100
  Profile = -> Sketch050
  Type = 0
FEATURE [Sketcher::SketchObject] Sketch052
  FullyConstrained = true
  MapMode = 5
  Placement = pos=(0,0,0) rot=(0.57735,0.57735,0.57735;2.0944rad)
  Support = -> [YZ_Plane018]
  sketch-geometry (8):
    g0: LineSegment StartX=-52 StartY=187 StartZ=0 EndX=60 EndY=187 EndZ=0
    g1: LineSegment StartX=60 StartY=187 StartZ=0 EndX=60 EndY=-57 EndZ=0
    g2: LineSegment StartX=60 StartY=-57 StartZ=0 EndX=-52 EndY=-57 EndZ=0
    g3: LineSegment StartX=-52 StartY=-57 StartZ=0 EndX=-52 EndY=187 EndZ=0
    g4: ArcOfCircle CenterX=4 CenterY=127 CenterZ=0 NormalX=0 NormalY=0 NormalZ=1 AngleXU=0 Radius=43.5 StartAngle=0 EndAngle=3.14159
    g5: ArcOfCircle CenterX=4 CenterY=3 CenterZ=0 NormalX=0 NormalY=0 NormalZ=1 AngleXU=0 Radius=43.5 StartAngle=3.14159 EndAngle=6.28319
    g6: LineSegment StartX=-39.5 StartY=127 StartZ=0 EndX=-39.5 EndY=3 EndZ=0
    g7: LineSegment StartX=47.5 StartY=127 StartZ=0 EndX=47.5 EndY=3 EndZ=0
  constraints (22):
    c: Coincident(g0,g1)
    c: Coincident(g1,g2)
    c: Coincident(g2,g3)
    c: Coincident(g3,g0)
    c: Horizontal(g0)
    c: Horizontal(g2)
    c: Vertical(g1)
    c: Vertical(g3)
    c: DistanceX(g-2,g1) = 60
    c: DistanceX(g0,g0) = 112
    c: DistanceY(g3,g3) = 244
    c: Distance(g2,g-1) = 57
    c: Tangent(g4,g7) = 1.5708
    c: Tangent(g4,g6) = -1.5708
    c: Tangent(g6,g5) = -1.5708
    c: Tangent(g7,g5) = 1.5708
    c: Vertical(g6)
    c: Equal(g4,g5)
    c: Distance(g4,g1) = 12.5
    c: Distance(g4,g3) = 12.5
    c: Distance(g4,g0) = 60
    c: Distance(g5,g2) = 60
FEATURE [PartDesign::Pad] Pad024
  Direction = (1,-2e-16,3e-16)
  Length = 10
  Length2 = 100
  Placement = pos=(0,0,0) rot=(0.57735,0.57735,0.57735;2.0944rad)
  Profile = -> Sketch052
  Type = 0
FEATURE [PartDesign::Body] Body018  label="fond"
  Group = -> [Sketch052,Pad024]
  Origin = -> Origin019
  Placement = pos=(-70,0,0) rot=(0,0,1;0rad)
  Tip = -> Pad024
FEATURE [Sketcher::SketchObject] Sketch053
  FullyConstrained = true
  MapMode = 5
  Support = -> [XY_Plane019]
  sketch-geometry (5):
    g0: LineSegment StartX=-70 StartY=60 StartZ=0 EndX=-70 EndY=-52 EndZ=0
    g1: LineSegment StartX=-70 StartY=-52 StartZ=0 EndX=143.261 EndY=-109.143 EndZ=0
    g2: LineSegment StartX=70 StartY=60 StartZ=0 EndX=-70 EndY=60 EndZ=0
    g3: Circle CenterX=0 CenterY=0 CenterZ=0 NormalX=0 NormalY=0 NormalZ=1 AngleXU=0 Radius=47.5
    g4: ArcOfCircle CenterX=0 CenterY=-70.7564 CenterZ=0 NormalX=0 NormalY=0 NormalZ=1 AngleXU=0 Radius=148.315 StartAngle=6.02139 EndAngle=7.36246
  constraints (14):
    c: Vertical(g0)
    c: Coincident(g0,g1)
    c: Coincident(g2,g0)
    c: Angle(g1,g-1) = 0.261799
    c: DistanceY(g-1,g2) = 60
    c: Coincident(g3,g-1)
    c: Radius(g3) = 47.5
    c: Symmetric(g0,g2,g-2)
    c: DistanceX(g2,g2) = 140
    c: DistanceY(g0,g0) = 112
    c: Coincident(g4,g2)
    c: Coincident(g4,g1)
    c: PointOnObject(g4,g-2)
    c: PointOnObject(g4,g1)
FEATURE [PartDesign::Pad] Pad025
  Direction = (0,0,1)
  Length = 10
  Length2 = 100
  Profile = -> Sketch053
  Type = 0
FEATURE [Sketcher::SketchObject] Sketch054
  ExternalGeometry = -> [Pad025]
  FullyConstrained = true
  MapMode = 5
  Placement = pos=(0,0,10) rot=(0,0,1;0rad)
  Support = -> [Pad025]
  sketch-geometry (4):
    g0: LineSegment StartX=-60 StartY=-54.6795 StartZ=0 EndX=-70 EndY=-54.6795 EndZ=0
    g1: LineSegment StartX=-70 StartY=-54.6795 StartZ=0 EndX=-70 EndY=60 EndZ=0
    g2: LineSegment StartX=-70 StartY=60 StartZ=0 EndX=-60 EndY=60 EndZ=0
    g3: LineSegment StartX=-60 StartY=60 StartZ=0 EndX=-60 EndY=-54.6795 EndZ=0
  constraints (11):
    c: Coincident(g0,g1)
    c: Coincident(g1,g2)
    c: Coincident(g2,g3)
    c: Coincident(g3,g0)
    c: Horizontal(g0)
    c: Horizontal(g2)
    c: Vertical(g1)
    c: Vertical(g3)
    c: PointOnObject(g0,g-4)
    c: Coincident(g1,g-3)
    c: DistanceX(g0,g0) = 10
FEATURE [PartDesign::Pocket] Pocket024
  BaseFeature = -> Pad025
  Length = 4
  Length2 = 100
  Profile = -> Sketch054
  Type = 0
FEATURE [Sketcher::SketchObject] Sketch055
  ExternalGeometry = -> [Pocket024]
  FullyConstrained = true
  MapMode = 5
  Placement = pos=(0,0,0) rot=(1,0,0;3.14159rad)
  Support = -> [Pocket024]
  sketch-geometry (3):
    g0: Circle CenterX=-65 CenterY=37.8106 CenterZ=0 NormalX=0 NormalY=0 NormalZ=1 AngleXU=0 Radius=1.55
    g1: Circle CenterX=-65 CenterY=-45 CenterZ=0 NormalX=0 NormalY=0 NormalZ=1 AngleXU=0 Radius=1.55
    g2: Circle CenterX=-65 CenterY=-3.5894 CenterZ=0 NormalX=0 NormalY=0 NormalZ=1 AngleXU=0 Radius=1.55
  constraints (9):
    c: Radius(g1) = 1.55
    c: Equal(g1,g2)
    c: Equal(g1,g0)
    c: Distance(g0,g-3) = 5
    c: Distance(g2,g-3) = 5
    c: Distance(g1,g-3) = 5
    c: Distance(g1,g-5) = 15
    c: Distance(g0,g-4) = 15
    c: Distance(g0,g2) = 41.4
FEATURE [PartDesign::Pocket] Pocket025
  BaseFeature = -> Pocket024
  Length = 10
  Length2 = 100
  Profile = -> Sketch055
  Type = 0
FEATURE [PartDesign::Body] Body019  label="cote_gauche"
  Group = -> [Sketch053,Pad025,Sketch054,Pocket024,Sketch055,Pocket025]
  Origin = -> Origin020
  Placement = pos=(0,0,-63) rot=(0,0,1;0rad)
  Tip = -> Pocket025
FEATURE [Sketcher::SketchObject] Sketch056
  ExternalGeometry = -> [Pad022]
  FullyConstrained = true
  MapMode = 5
  Placement = pos=(0,0,10) rot=(0,0,1;0rad)
  Support = -> [Pad022]
  sketch-geometry (3):
    g0: Circle CenterX=-65 CenterY=45 CenterZ=0 NormalX=0 NormalY=0 NormalZ=1 AngleXU=0 Radius=1.55
    g1: Circle CenterX=-65 CenterY=3.5894 CenterZ=0 NormalX=0 NormalY=0 NormalZ=1 AngleXU=0 Radius=1.55
    g2: Circle CenterX=-65 CenterY=-37.8106 CenterZ=0 NormalX=0 NormalY=0 NormalZ=1 AngleXU=0 Radius=1.55
  constraints (9):
    c: Radius(g1) = 1.55
    c: Equal(g1,g2)
    c: Equal(g1,g0)
    c: Distance(g0,g-3) = 5
    c: Distance(g1,g-3) = 5
    c: Distance(g2,g-3) = 5
    c: Distance(g2,g-4) = 15
    c: Distance(g2,g1) = 41.4
    c: Distance(g0,g-5) = 15
FEATURE [PartDesign::Pocket] Pocket026
  BaseFeature = -> Pad022
  Length = 16
  Length2 = 100
  Profile = -> Sketch056
  Type = 0
FEATURE [Sketcher::SketchObject] Sketch057
  ExternalGeometry = -> [Pocket026]
  FullyConstrained = true
  MapMode = 5
  Placement = pos=(0,0,0) rot=(1,0,0;3.14159rad)
  Support = -> [Pocket026]
  sketch-geometry (4):
    g0: LineSegment StartX=-60 StartY=54.6795 StartZ=0 EndX=-70 EndY=54.6795 EndZ=0
    g1: LineSegment StartX=-70 StartY=54.6795 StartZ=0 EndX=-70 EndY=-60 EndZ=0
    g2: LineSegment StartX=-70 StartY=-60 StartZ=0 EndX=-60 EndY=-60 EndZ=0
    g3: LineSegment StartX=-60 StartY=-60 StartZ=0 EndX=-60 EndY=54.6795 EndZ=0
  constraints (11):
    c: Coincident(g0,g1)
    c: Coincident(g1,g2)
    c: Coincident(g2,g3)
    c: Coincident(g3,g0)
    c: Horizontal(g0)
    c: Horizontal(g2)
    c: Vertical(g1)
    c: Vertical(g3)
    c: PointOnObject(g0,g-4)
    c: Coincident(g1,g-5)
    c: DistanceX(g2,g2) = 10
FEATURE [PartDesign::Pocket] Pocket027
  BaseFeature = -> Pocket026
  Length = 4
  Length2 = 100
  Profile = -> Sketch057
  Type = 0
FEATURE [PartDesign::Body] Body016  label="cote_droit"
  Group = -> [Sketch050,Pad022,Sketch056,Pocket026,Sketch057,Pocket027]
  Origin = -> Origin017
  Placement = pos=(0,0,183) rot=(0,0,1;0rad)
  Tip = -> Pocket027
FEATURE [TechDraw::DrawSVGTemplate] Template
  Height = 297
  Orientation = 1
  Width = 420
FEATURE [TechDraw::DrawViewPart] View
  CoarseView = false
  Direction = (1,0,0)
  Focus = 100
  HardHidden = false
  IsoCount = 0
  IsoHidden = false
  IsoVisible = false
  LockPosition = false
  Perspective = false
  Rotation = 0
  ScaleType = 0
  SeamHidden = false
  SeamVisible = true
  SmoothHidden = false
  SmoothVisible = true
  Source = -> [Body018]
  X = 210
  XDirection = (0,1,0)
  Y = 148.5
FEATURE [TechDraw::DrawPage] Page
  KeepUpdated = true
  NextBalloonIndex = 1
  ProjectionType = 0
  Template = -> Template
  Views = -> [View]
FEATURE [TechDraw::DrawSVGTemplate] Template001
  Height = 297
  Orientation = 1
  Width = 420
FEATURE [TechDraw::DrawViewPart] View001
  CoarseView = false
  Direction = (0,0,1)
  Focus = 100
  HardHidden = false
  IsoCount = 0
  IsoHidden = false
  IsoVisible = false
  LockPosition = false
  Perspective = false
  Rotation = 0
  ScaleType = 0
  SeamHidden = false
  SeamVisible = true
  SmoothHidden = false
  SmoothVisible = true
  Source = -> [Body019]
  X = 210
  XDirection = (1,0,0)
  Y = 148.5
FEATURE [TechDraw::DrawPage] Page001
  KeepUpdated = true
  NextBalloonIndex = 1
  ProjectionType = 0
  Template = -> Template001
  Views = -> [View001]
FEATURE [TechDraw::DrawSVGTemplate] Template002
  Height = 297
  Orientation = 1
  Width = 420
FEATURE [Sketcher::SketchObject] Sketch049
  FullyConstrained = true
  MapMode = 5
  Placement = pos=(0,0,0) rot=(1,0,0;1.5708rad)
  Support = -> [XZ_Plane015]
  sketch-geometry (4):
    g0: LineSegment StartX=-130 StartY=215 StartZ=0 EndX=130 EndY=215 EndZ=0
    g1: LineSegment StartX=130 StartY=215 StartZ=0 EndX=130 EndY=-85 EndZ=0
    g2: LineSegment StartX=130 StartY=-85 StartZ=0 EndX=-130 EndY=-85 EndZ=0
    g3: LineSegment StartX=-130 StartY=-85 StartZ=0 EndX=-130 EndY=215 EndZ=0
  constraints (11):
    c: Coincident(g0,g1)
    c: Coincident(g1,g2)
    c: Coincident(g2,g3)
    c: Coincident(g3,g0)
    c: Horizontal(g2)
    c: Vertical(g1)
    c: Vertical(g3)
    c: DistanceX(g0,g0) = 260
    c: DistanceY(g1,g1) = 300
    c: Symmetric(g0,g0,g-2)
    c: DistanceY(g-1,g2) = -85
FEATURE [PartDesign::Pad] Pad021
  Direction = (0,-1,2e-16)
  Length = 12
  Length2 = 100
  Placement = pos=(0,0,0) rot=(1,0,0;1.5708rad)
  Profile = -> Sketch049
  Type = 0
FEATURE [PartDesign::Fillet] Fillet023
  Base = -> Pad021 [Edge2,Edge1,Edge8,Edge5]
  BaseFeature = -> Pad021
  Placement = pos=(0,0,0) rot=(1,0,0;1.5708rad)
  Radius = 30
  SupportTransform = false
FEATURE [Sketcher::SketchObject] Sketch058
  ExternalGeometry = -> [Fillet023]
  FullyConstrained = true
  MapMode = 5
  Placement = pos=(0,0,0) rot=(-1,0,0;1.5708rad)
  Support = -> [Fillet023]
  sketch-geometry (8):
    g0: LineSegment StartX=110.5 StartY=63 StartZ=0 EndX=-110.5 EndY=63 EndZ=0
    g1: LineSegment StartX=-110.5 StartY=-193 StartZ=0 EndX=110.5 EndY=-193 EndZ=0
    g2: LineSegment StartX=110.5 StartY=-193 StartZ=0 EndX=110.5 EndY=63 EndZ=0
    g3: LineSegment StartX=100.5 StartY=53 StartZ=0 EndX=100.5 EndY=-183 EndZ=0
    g4: LineSegment StartX=-110.5 StartY=63 StartZ=0 EndX=-110.5 EndY=-193 EndZ=0
    g5: LineSegment StartX=100.5 StartY=-183 StartZ=0 EndX=-100.5 EndY=-183 EndZ=0
    g6: LineSegment StartX=-100.5 StartY=-183 StartZ=0 EndX=-100.5 EndY=53 EndZ=0
    g7: LineSegment StartX=-100.5 StartY=53 StartZ=0 EndX=100.5 EndY=53 EndZ=0
  constraints (22):
    c: Coincident(g1,g2)
    c: Vertical(g2)
    c: DistanceX(g0,g0) = 221
    c: Symmetric(g0,g0,g-2)
    c: Symmetric(g1,g1,g-2)
    c: Distance(g0,g-3) = 22
    c: Coincident(g2,g0)
    c: Vertical(g3)
    c: Distance(g3,g2) = 10
    c: DistanceY(g3,g3) = 236
    c: Coincident(g0,g4)
    c: Coincident(g4,g1)
    c: Coincident(g3,g5)
    c: Horizontal(g5)
    c: Coincident(g5,g6)
    c: Vertical(g6)
    c: Coincident(g6,g7)
    c: Coincident(g7,g3)
    c: Horizontal(g7)
    c: Distance(g6,g4) = 10
    c: Distance(g6,g0) = 10
    c: Distance(g5,g1) = 10
FEATURE [PartDesign::Pocket] Pocket028
  BaseFeature = -> Fillet023
  Length = 4
  Length2 = 100
  Placement = pos=(0,0,0) rot=(1,0,0;1.5708rad)
  Profile = -> Sketch058
  Type = 0
FEATURE [PartDesign::Body] Body015  label="toit"
  Group = -> [Sketch049,Pad021,Fillet023,Sketch058,Pocket028]
  Origin = -> Origin016
  Placement = pos=(36.7052,-79.8351,0) rot=(0,0,-1;0.261799rad)
  Tip = -> Pocket028
FEATURE [TechDraw::DrawViewPart] View002
  CoarseView = false
  Direction = (0,1,0)
  Focus = 100
  HardHidden = false
  IsoCount = 0
  IsoHidden = false
  IsoVisible = false
  LockPosition = false
  Perspective = false
  Rotation = 0
  ScaleType = 0
  SeamHidden = false
  SeamVisible = true
  SmoothHidden = false
  SmoothVisible = true
  Source = -> [Body015]
  X = 210
  XDirection = (-1,0,0)
  Y = 148.5
FEATURE [TechDraw::DrawPage] Page002
  KeepUpdated = true
  NextBalloonIndex = 1
  ProjectionType = 0
  Template = -> Template002
  Views = -> [View002]
